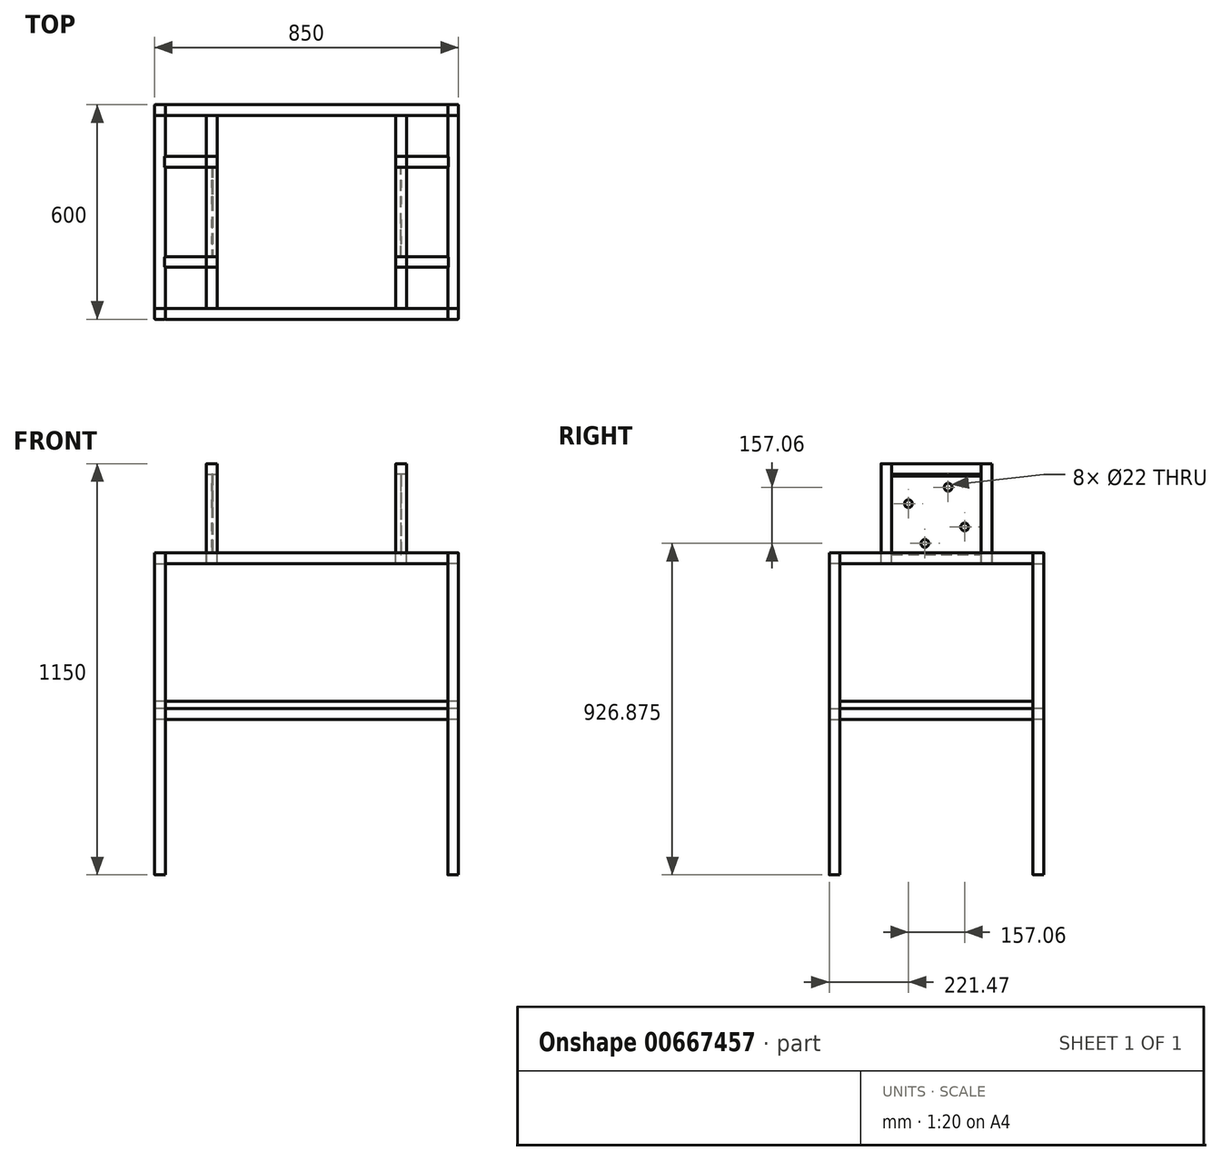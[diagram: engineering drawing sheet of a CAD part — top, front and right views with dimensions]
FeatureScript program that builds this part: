
annotation { "Feature Type Name" : "Feature", "Feature Type Description" : "" }
export const myFeature = defineFeature(function(context is Context, id is Id, definition is map)
    precondition{}
    {
        {
            var Q0;
            Q0=qCreatedBy(makeId("Top.planeOp"),FACE);
            var sketch = newSketch(context, id + "F0", { "sketchPlane" : qUnion([Q0])});
            skLineSegment(sketch, "E0.bottom", {"start": v(410, 285) * mm, "end": v(-410, 285) * mm, "construction": true});
            skLineSegment(sketch, "E0.left", {"start": v(410, 285) * mm, "end": v(410, -285) * mm, "construction": true});
            skLineSegment(sketch, "E0.right", {"start": v(-410, 285) * mm, "end": v(-410, -285) * mm, "construction": true});
            skPoint(sketch, "E0.middle", {"position": v(0, 0) * mm});
            skLineSegment(sketch, "E1.bottom", {"start": v(-395, 300) * mm, "end": v(-425, 300) * mm});
            skLineSegment(sketch, "E1.top", {"start": v(-395, 270) * mm, "end": v(-425, 270) * mm});
            skLineSegment(sketch, "E1.left", {"start": v(-395, 300) * mm, "end": v(-395, 270) * mm});
            skLineSegment(sketch, "E1.right", {"start": v(-425, 300) * mm, "end": v(-425, 270) * mm});
            skPoint(sketch, "E1.middle", {"position": v(-410, 285) * mm});
            skLineSegment(sketch, "E2", {"start": v(0, 0) * mm, "end": v(0, 285) * mm, "construction": true});
            skLineSegment(sketch, "E3", {"start": v(-410, 0) * mm, "end": v(410, 0) * mm, "construction": true});
            skLineSegment(sketch, "E4.MirrorCS", {"start": v(395, 270) * mm, "end": v(425, 270) * mm});
            skLineSegment(sketch, "E5.MirrorCS", {"start": v(395, 300) * mm, "end": v(395, 270) * mm});
            skLineSegment(sketch, "E6.MirrorCS", {"start": v(425, 300) * mm, "end": v(425, 270) * mm});
            skLineSegment(sketch, "E7.MirrorCS", {"start": v(395, 300) * mm, "end": v(425, 300) * mm});
            skLineSegment(sketch, "E8.MirrorCS", {"start": v(-395, -300) * mm, "end": v(-425, -300) * mm});
            skLineSegment(sketch, "E9.MirrorCS", {"start": v(-425, -300) * mm, "end": v(-425, -270) * mm});
            skLineSegment(sketch, "E10.MirrorCS", {"start": v(-395, -270) * mm, "end": v(-425, -270) * mm});
            skLineSegment(sketch, "E11.MirrorCS", {"start": v(-395, -300) * mm, "end": v(-395, -270) * mm});
            skLineSegment(sketch, "E12.MirrorCS", {"start": v(395, -270) * mm, "end": v(425, -270) * mm});
            skLineSegment(sketch, "E13.MirrorCS", {"start": v(395, -300) * mm, "end": v(395, -270) * mm});
            skLineSegment(sketch, "E14.MirrorCS", {"start": v(395, -300) * mm, "end": v(425, -300) * mm});
            skLineSegment(sketch, "E15.MirrorCS", {"start": v(425, -300) * mm, "end": v(425, -270) * mm});
            skSolve(sketch);
        }
        {
            var Q0;
            Q0 = qSketchRegion(id + "F0", true);
            extrude(context, id + "F1", {"entities" : qUnion([Q0]), "oppositeDirection" : true, "depth" : 900 * mm, "offsetDistance" : 25 * mm});
        }
        {
            var Q0;
            Q0=makeQuery(id+"F1.opExtrude","SWEPT_FACE",FACE,{"disambiguationData":[OSD([sQuery(id+"F0.wireOp",EDGE,"E13.MirrorCS")])]});
            var sketch = newSketch(context, id + "F2", { "sketchPlane" : qUnion([Q0])});
            skLineSegment(sketch, "E16.bottom", {"start": v(270, -465) * mm, "end": v(300, -465) * mm});
            skLineSegment(sketch, "E16.top", {"start": v(270, -435) * mm, "end": v(300, -435) * mm});
            skLineSegment(sketch, "E16.left", {"start": v(270, -465) * mm, "end": v(270, -435) * mm});
            skLineSegment(sketch, "E16.right", {"start": v(300, -465) * mm, "end": v(300, -435) * mm});
            skPoint(sketch, "E16.middle", {"position": v(285, -450) * mm});
            skSolve(sketch);
        }
        {
            var Q0;
            Q0 = qSketchRegion(id + "F2", true);
            extrude(context, id + "F3", {"entities" : qUnion([Q0]), "endBound" : BoundingType.UP_TO_NEXT, "depth" : 782 * mm, "offsetDistance" : 25 * mm});
        }
        {
            var Q0;
            Q0=makeQuery(id+"F1.opExtrude","SWEPT_FACE",FACE,{"disambiguationData":[OSD([sQuery(id+"F0.wireOp",EDGE,"E12.MirrorCS")])]});
            var sketch = newSketch(context, id + "F4", { "sketchPlane" : qUnion([Q0])});
            skLineSegment(sketch, "E17.bottom", {"start": v(-395, -465) * mm, "end": v(-425, -465) * mm});
            skLineSegment(sketch, "E17.top", {"start": v(-395, -435) * mm, "end": v(-425, -435) * mm});
            skLineSegment(sketch, "E17.left", {"start": v(-395, -465) * mm, "end": v(-395, -435) * mm});
            skLineSegment(sketch, "E17.right", {"start": v(-425, -465) * mm, "end": v(-425, -435) * mm});
            skSolve(sketch);
        }
        {
            var Q0;
            Q0=makeQuery(id+"F4.imprint","IMPRINT",FACE,{"disambiguationData":[TD([[makeQuery(id+"F4.imprint","IMPRINT",EDGE,{"derivedFrom":sQuery(id+"F4.wireOp",EDGE,"E17.bottom")}),-1.0]])]});
            extrude(context, id + "F5", {"entities" : qUnion([Q0]), "endBound" : BoundingType.UP_TO_NEXT, "depth" : 25 * mm, "offsetDistance" : 25 * mm});
        }
        {
            var Q0;
            Q0=makeQuery(id+"F1.opExtrude","SWEPT_FACE",FACE,{"disambiguationData":[OSD([sQuery(id+"F0.wireOp",EDGE,"E5.MirrorCS")])]});
            var sketch = newSketch(context, id + "F6", { "sketchPlane" : qUnion([Q0])});
            skLineSegment(sketch, "E18.bottom", {"start": v(-300, -435) * mm, "end": v(-270, -435) * mm});
            skLineSegment(sketch, "E18.top", {"start": v(-300, -465) * mm, "end": v(-270, -465) * mm});
            skLineSegment(sketch, "E18.left", {"start": v(-300, -435) * mm, "end": v(-300, -465) * mm});
            skLineSegment(sketch, "E18.right", {"start": v(-270, -435) * mm, "end": v(-270, -465) * mm});
            skSolve(sketch);
        }
        {
            var Q0;
            Q0=makeQuery(id+"F6.imprint","IMPRINT",FACE,{"disambiguationData":[TD([[makeQuery(id+"F6.imprint","IMPRINT",EDGE,{"derivedFrom":sQuery(id+"F6.wireOp",EDGE,"E18.bottom")}),-1.0]])]});
            extrude(context, id + "F7", {"entities" : qUnion([Q0]), "endBound" : BoundingType.UP_TO_NEXT, "depth" : 25 * mm, "offsetDistance" : 25 * mm});
        }
        {
            var Q0;
            Q0=makeQuery(id+"F1.opExtrude","SWEPT_FACE",FACE,{"disambiguationData":[OSD([sQuery(id+"F0.wireOp",EDGE,"E10.MirrorCS")])]});
            var sketch = newSketch(context, id + "F8", { "sketchPlane" : qUnion([Q0])});
            skLineSegment(sketch, "E19.bottom", {"start": v(395, -435) * mm, "end": v(425, -435) * mm});
            skLineSegment(sketch, "E19.top", {"start": v(395, -465) * mm, "end": v(425, -465) * mm});
            skLineSegment(sketch, "E19.left", {"start": v(395, -435) * mm, "end": v(395, -465) * mm});
            skLineSegment(sketch, "E19.right", {"start": v(425, -435) * mm, "end": v(425, -465) * mm});
            skSolve(sketch);
        }
        {
            var Q0;
            Q0=makeQuery(id+"F8.imprint","IMPRINT",FACE,{"disambiguationData":[TD([[makeQuery(id+"F8.imprint","IMPRINT",EDGE,{"derivedFrom":sQuery(id+"F8.wireOp",EDGE,"E19.bottom")}),-1.0]])]});
            extrude(context, id + "F9", {"entities" : qUnion([Q0]), "endBound" : BoundingType.UP_TO_NEXT, "depth" : 25 * mm, "offsetDistance" : 25 * mm});
        }
        {
            var Q0;
            Q0=makeQuery(id+"F1.opExtrude","SWEPT_FACE",FACE,{"disambiguationData":[OSD([sQuery(id+"F0.wireOp",EDGE,"E4.MirrorCS")])]});
            var sketch = newSketch(context, id + "F10", { "sketchPlane" : qUnion([Q0])});
            skLineSegment(sketch, "E20.bottom", {"start": v(425, -900) * mm, "end": v(395, -900) * mm});
            skLineSegment(sketch, "E20.top", {"start": v(425, -870) * mm, "end": v(395, -870) * mm});
            skLineSegment(sketch, "E20.left", {"start": v(425, -900) * mm, "end": v(425, -870) * mm});
            skLineSegment(sketch, "E20.right", {"start": v(395, -900) * mm, "end": v(395, -870) * mm});
            skSolve(sketch);
        }
        {
            var Q0;
            Q0 = qSketchRegion(id + "F10", true);
            extrude(context, id + "F11", {"entities" : qUnion([Q0]), "endBound" : BoundingType.UP_TO_NEXT, "depth" : 25 * mm, "offsetDistance" : 25 * mm});
        }
        {
            var Q0;
            Q0=makeQuery(id+"F1.opExtrude","SWEPT_FACE",FACE,{"disambiguationData":[OSD([sQuery(id+"F0.wireOp",EDGE,"E13.MirrorCS")])]});
            var sketch = newSketch(context, id + "F12", { "sketchPlane" : qUnion([Q0])});
            skLineSegment(sketch, "E21.bottom", {"start": v(300, -900) * mm, "end": v(270, -900) * mm});
            skLineSegment(sketch, "E21.top", {"start": v(300, -870) * mm, "end": v(270, -870) * mm});
            skLineSegment(sketch, "E21.left", {"start": v(300, -900) * mm, "end": v(300, -870) * mm});
            skLineSegment(sketch, "E21.right", {"start": v(270, -900) * mm, "end": v(270, -870) * mm});
            skSolve(sketch);
        }
        {
            var Q0;
            Q0 = qSketchRegion(id + "F12", true);
            extrude(context, id + "F13", {"entities" : qUnion([Q0]), "endBound" : BoundingType.UP_TO_NEXT, "depth" : 25 * mm, "offsetDistance" : 25 * mm});
        }
        {
            var Q0;
            Q0=makeQuery(id+"F1.opExtrude","SWEPT_FACE",FACE,{"disambiguationData":[OSD([sQuery(id+"F0.wireOp",EDGE,"E10.MirrorCS")])]});
            var sketch = newSketch(context, id + "F14", { "sketchPlane" : qUnion([Q0])});
            skLineSegment(sketch, "E22.bottom", {"start": v(425, -900) * mm, "end": v(395, -900) * mm});
            skLineSegment(sketch, "E22.top", {"start": v(425, -870) * mm, "end": v(395, -870) * mm});
            skLineSegment(sketch, "E22.left", {"start": v(425, -900) * mm, "end": v(425, -870) * mm});
            skLineSegment(sketch, "E22.right", {"start": v(395, -900) * mm, "end": v(395, -870) * mm});
            skSolve(sketch);
        }
        {
            var Q0;
            Q0 = qSketchRegion(id + "F14", true);
            var Q1;
            Q1=makeQuery(id+"F14.imprint","IMPRINT",FACE,{"disambiguationData":[TD([[makeQuery(id+"F14.imprint","IMPRINT",EDGE,{"derivedFrom":sQuery(id+"F14.wireOp",EDGE,"E22.bottom")}),1.0]])]});
            extrude(context, id + "F15", {"entities" : qUnion([Q0, Q1]), "endBound" : BoundingType.UP_TO_NEXT, "depth" : 25 * mm, "offsetDistance" : 25 * mm});
        }
        {
            var Q0;
            Q0=makeQuery(id+"F1.opExtrude","SWEPT_FACE",FACE,{"disambiguationData":[OSD([sQuery(id+"F0.wireOp",EDGE,"E1.left")])]});
            var sketch = newSketch(context, id + "F16", { "sketchPlane" : qUnion([Q0])});
            skLineSegment(sketch, "E23.bottom", {"start": v(300, -900) * mm, "end": v(270, -900) * mm});
            skLineSegment(sketch, "E23.top", {"start": v(300, -870) * mm, "end": v(270, -870) * mm});
            skLineSegment(sketch, "E23.left", {"start": v(300, -900) * mm, "end": v(300, -870) * mm});
            skLineSegment(sketch, "E23.right", {"start": v(270, -900) * mm, "end": v(270, -870) * mm});
            skSolve(sketch);
        }
        {
            var Q0;
            Q0 = qSketchRegion(id + "F16", true);
            var Q1;
            Q1=makeQuery(id+"F16.imprint","IMPRINT",FACE,{"disambiguationData":[TD([[makeQuery(id+"F16.imprint","IMPRINT",EDGE,{"derivedFrom":sQuery(id+"F16.wireOp",EDGE,"E23.bottom")}),-1.0]])]});
            extrude(context, id + "F17", {"entities" : qUnion([Q0, Q1]), "endBound" : BoundingType.UP_TO_NEXT, "depth" : 25 * mm, "offsetDistance" : 25 * mm});
        }
        {
            var Q0;
            Q0=makeQuery(id+"F13.opExtrude","SWEPT_FACE",FACE,{"disambiguationData":[OSD([sQuery(id+"F12.wireOp",EDGE,"E21.right")])]});
            var sketch = newSketch(context, id + "F18", { "sketchPlane" : qUnion([Q0])});
            skLineSegment(sketch, "E24.bottom", {"start": v(280, -900) * mm, "end": v(250, -900) * mm});
            skLineSegment(sketch, "E24.top", {"start": v(280, -870) * mm, "end": v(250, -870) * mm});
            skLineSegment(sketch, "E24.left", {"start": v(280, -900) * mm, "end": v(280, -870) * mm});
            skLineSegment(sketch, "E24.right", {"start": v(250, -900) * mm, "end": v(250, -870) * mm});
            skLineSegment(sketch, "E25.bottom", {"start": v(-250, -900) * mm, "end": v(-280, -900) * mm});
            skLineSegment(sketch, "E25.top", {"start": v(-250, -870) * mm, "end": v(-280, -870) * mm});
            skLineSegment(sketch, "E25.left", {"start": v(-250, -900) * mm, "end": v(-250, -870) * mm});
            skLineSegment(sketch, "E25.right", {"start": v(-280, -900) * mm, "end": v(-280, -870) * mm});
            skSolve(sketch);
        }
        {
            var Q0;
            Q0=makeQuery(id+"F18.imprint","IMPRINT",FACE,{"disambiguationData":[TD([[makeQuery(id+"F18.imprint","IMPRINT",EDGE,{"derivedFrom":sQuery(id+"F18.wireOp",EDGE,"E24.bottom")}),-1.0]])]});
            var Q1;
            Q1=makeQuery(id+"F18.imprint","IMPRINT",FACE,{"disambiguationData":[TD([[makeQuery(id+"F18.imprint","IMPRINT",EDGE,{"derivedFrom":sQuery(id+"F18.wireOp",EDGE,"E25.bottom")}),-1.0]])]});
            extrude(context, id + "F19", {"entities" : qUnion([Q0, Q1]), "endBound" : BoundingType.UP_TO_NEXT, "depth" : 25 * mm, "offsetDistance" : 25 * mm});
        }
        {
            var Q0;
            Q0=makeQuery(id+"F19.opExtrude","SWEPT_FACE",FACE,{"disambiguationData":[OSD([sQuery(id+"F18.wireOp",EDGE,"E24.right")])]});
            var sketch = newSketch(context, id + "F20", { "sketchPlane" : qUnion([Q0])});
            skLineSegment(sketch, "E26.bottom", {"start": v(155, -900) * mm, "end": v(125, -900) * mm});
            skLineSegment(sketch, "E26.top", {"start": v(155, -870) * mm, "end": v(125, -870) * mm});
            skLineSegment(sketch, "E26.left", {"start": v(155, -900) * mm, "end": v(155, -870) * mm});
            skLineSegment(sketch, "E26.right", {"start": v(125, -900) * mm, "end": v(125, -870) * mm});
            skLineSegment(sketch, "E27.bottom", {"start": v(-125, -900) * mm, "end": v(-155, -900) * mm});
            skLineSegment(sketch, "E27.top", {"start": v(-125, -870) * mm, "end": v(-155, -870) * mm});
            skLineSegment(sketch, "E27.left", {"start": v(-125, -900) * mm, "end": v(-125, -870) * mm});
            skLineSegment(sketch, "E27.right", {"start": v(-155, -900) * mm, "end": v(-155, -870) * mm});
            skSolve(sketch);
        }
        {
            var Q0;
            Q0=makeQuery(id+"F19.opExtrude","SWEPT_FACE",FACE,{"disambiguationData":[OSD([sQuery(id+"F18.wireOp",EDGE,"E24.bottom")])]});
            var sketch = newSketch(context, id + "F21", { "sketchPlane" : qUnion([Q0])});
            skLineSegment(sketch, "E28.bottom", {"start": v(-250, 155) * mm, "end": v(-280, 155) * mm});
            skLineSegment(sketch, "E28.top", {"start": v(-250, 125) * mm, "end": v(-280, 125) * mm});
            skLineSegment(sketch, "E28.left", {"start": v(-250, 155) * mm, "end": v(-250, 125) * mm});
            skLineSegment(sketch, "E28.right", {"start": v(-280, 155) * mm, "end": v(-280, 125) * mm});
            skLineSegment(sketch, "E29.bottom", {"start": v(-250, -125) * mm, "end": v(-280, -125) * mm});
            skLineSegment(sketch, "E29.top", {"start": v(-250, -155) * mm, "end": v(-280, -155) * mm});
            skLineSegment(sketch, "E29.left", {"start": v(-250, -125) * mm, "end": v(-250, -155) * mm});
            skLineSegment(sketch, "E29.right", {"start": v(-280, -125) * mm, "end": v(-280, -155) * mm});
            skSolve(sketch);
        }
        {
            var Q0;
            Q0=makeQuery(id+"F19.opExtrude","SWEPT_FACE",FACE,{"disambiguationData":[OSD([sQuery(id+"F18.wireOp",EDGE,"E25.bottom")])]});
            var sketch = newSketch(context, id + "F22", { "sketchPlane" : qUnion([Q0])});
            skLineSegment(sketch, "E30.bottom", {"start": v(250, -125) * mm, "end": v(280, -125) * mm});
            skLineSegment(sketch, "E30.top", {"start": v(250, -155) * mm, "end": v(280, -155) * mm});
            skLineSegment(sketch, "E30.left", {"start": v(250, -125) * mm, "end": v(250, -155) * mm});
            skLineSegment(sketch, "E30.right", {"start": v(280, -125) * mm, "end": v(280, -155) * mm});
            skLineSegment(sketch, "E31.bottom", {"start": v(250, 155) * mm, "end": v(280, 155) * mm});
            skLineSegment(sketch, "E31.top", {"start": v(250, 125) * mm, "end": v(280, 125) * mm});
            skLineSegment(sketch, "E31.left", {"start": v(250, 155) * mm, "end": v(250, 125) * mm});
            skLineSegment(sketch, "E31.right", {"start": v(280, 155) * mm, "end": v(280, 125) * mm});
            skSolve(sketch);
        }
        {
            var Q0;
            Q0=makeQuery(id+"F21.imprint","IMPRINT",FACE,{"disambiguationData":[TD([[makeQuery(id+"F21.imprint","IMPRINT",EDGE,{"derivedFrom":sQuery(id+"F21.wireOp",EDGE,"E28.bottom")}),1.0]])]});
            var Q1;
            Q1=makeQuery(id+"F22.imprint","IMPRINT",FACE,{"disambiguationData":[TD([[makeQuery(id+"F22.imprint","IMPRINT",EDGE,{"derivedFrom":sQuery(id+"F22.wireOp",EDGE,"E31.bottom")}),-1.0]])]});
            var Q2;
            Q2=makeQuery(id+"F21.imprint","IMPRINT",FACE,{"disambiguationData":[TD([[makeQuery(id+"F21.imprint","IMPRINT",EDGE,{"derivedFrom":sQuery(id+"F21.wireOp",EDGE,"E29.bottom")}),1.0]])]});
            var Q3;
            Q3=makeQuery(id+"F22.imprint","IMPRINT",FACE,{"disambiguationData":[TD([[makeQuery(id+"F22.imprint","IMPRINT",EDGE,{"derivedFrom":sQuery(id+"F22.wireOp",EDGE,"E30.bottom")}),-1.0]])]});
            extrude(context, id + "F23", {"entities" : qUnion([Q0, Q1, Q2, Q3]), "depth" : 250 * mm, "offsetDistance" : 25 * mm});
        }
        {
            var Q0;
            Q0=makeQuery(id+"F23.opExtrude","SWEPT_FACE",FACE,{"disambiguationData":[OSD([sQuery(id+"F21.wireOp",EDGE,"E29.bottom")])]});
            var sketch = newSketch(context, id + "F24", { "sketchPlane" : qUnion([Q0])});
            skLineSegment(sketch, "E32.bottom", {"start": v(-250, -1150) * mm, "end": v(-280, -1150) * mm});
            skLineSegment(sketch, "E32.top", {"start": v(-250, -1120) * mm, "end": v(-280, -1120) * mm});
            skLineSegment(sketch, "E32.left", {"start": v(-250, -1150) * mm, "end": v(-250, -1120) * mm});
            skLineSegment(sketch, "E32.right", {"start": v(-280, -1150) * mm, "end": v(-280, -1120) * mm});
            skSolve(sketch);
        }
        {
            var Q0;
            Q0=makeQuery(id+"F24.imprint","IMPRINT",FACE,{"disambiguationData":[TD([[makeQuery(id+"F24.imprint","IMPRINT",EDGE,{"derivedFrom":sQuery(id+"F24.wireOp",EDGE,"E32.bottom")}),-1.0]])]});
            extrude(context, id + "F25", {"entities" : qUnion([Q0]), "endBound" : BoundingType.UP_TO_NEXT, "depth" : 25 * mm, "offsetDistance" : 25 * mm});
        }
        {
            var Q0;
            Q0=makeQuery(id+"F23.opExtrude","SWEPT_FACE",FACE,{"disambiguationData":[OSD([sQuery(id+"F22.wireOp",EDGE,"E30.bottom")])]});
            var sketch = newSketch(context, id + "F26", { "sketchPlane" : qUnion([Q0])});
            skLineSegment(sketch, "E33.bottom", {"start": v(280, -1150) * mm, "end": v(250, -1150) * mm});
            skLineSegment(sketch, "E33.top", {"start": v(280, -1120) * mm, "end": v(250, -1120) * mm});
            skLineSegment(sketch, "E33.left", {"start": v(280, -1150) * mm, "end": v(280, -1120) * mm});
            skLineSegment(sketch, "E33.right", {"start": v(250, -1150) * mm, "end": v(250, -1120) * mm});
            skSolve(sketch);
        }
        {
            var Q0;
            Q0=makeQuery(id+"F26.imprint","IMPRINT",FACE,{"disambiguationData":[TD([[makeQuery(id+"F26.imprint","IMPRINT",EDGE,{"derivedFrom":sQuery(id+"F26.wireOp",EDGE,"E33.bottom")}),1.0]])]});
            extrude(context, id + "F27", {"entities" : qUnion([Q0]), "endBound" : BoundingType.UP_TO_NEXT, "depth" : 25 * mm, "offsetDistance" : 25 * mm});
        }
        {
            var Q0;
            Q0=makeQuery(id+"F23.opExtrude","CAP_EDGE",EDGE,{"disambiguationData":[OSD([sQuery(id+"F22.wireOp",EDGE,"E30.bottom")])],"isStart":true});
            cPoint(context, id + "F28", {"entities" : qUnion([Q0]), "parameter" : 0.5});
        }
        {
            var Q0;
            Q0=makeQuery(id+"F27.opExtrude","CAP_EDGE",EDGE,{"disambiguationData":[OSD([sQuery(id+"F26.wireOp",EDGE,"E33.top")])],"isStart":false});
            cPoint(context, id + "F29", {"entities" : qUnion([Q0]), "parameter" : 0.5});
        }
        {
            var Q0;
            Q0=makeQuery(id+"F27.opExtrude","CAP_EDGE",EDGE,{"disambiguationData":[OSD([sQuery(id+"F26.wireOp",EDGE,"E33.top")])],"isStart":true});
            cPoint(context, id + "F30", {"entities" : qUnion([Q0]), "parameter" : 0.5});
        }
        {
            var Q0;
            Q0 = qCreatedBy(id + "F28" ,VERTEX);
            var Q1;
            Q1 = qCreatedBy(id + "F29" ,VERTEX);
            var Q2;
            Q2 = qCreatedBy(id + "F30" ,VERTEX);
            cPlane(context, id + "F31", {"entities" : qUnion([Q0, Q1, Q2]), "cplaneType" : CPlaneType.THREE_POINT, "offset" : 25 * mm, "width" : 150 * mm, "height" : 150 * mm});
        }
        {
            var Q0;
            Q0=qCreatedBy(id+"F31.planeOp",FACE);
            var sketch = newSketch(context, id + "F32", { "sketchPlane" : qUnion([Q0])});
            skLineSegment(sketch, "E34.bottom", {"start": v(-125, -1115.4) * mm, "end": v(125, -1115.4) * mm});
            skLineSegment(sketch, "E34.top", {"start": v(-125, -895.4) * mm, "end": v(125, -895.4) * mm});
            skLineSegment(sketch, "E34.left", {"start": v(-125, -1115.4) * mm, "end": v(-125, -895.4) * mm});
            skLineSegment(sketch, "E34.right", {"start": v(125, -1115.4) * mm, "end": v(125, -895.4) * mm});
            skSolve(sketch);
        }
        {
            var Q0;
            Q0=makeQuery(id+"F32.imprint","IMPRINT",FACE,{"disambiguationData":[TD([[makeQuery(id+"F32.imprint","IMPRINT",EDGE,{"derivedFrom":sQuery(id+"F32.wireOp",EDGE,"E34.bottom")}),1.0]])]});
            extrude(context, id + "F33", {"entities" : qUnion([Q0]), "depth" : 2 * mm, "offsetDistance" : 25 * mm});
        }
        {
            var Q0;
            Q0=makeQuery(id+"F33.opExtrude","SWEPT_FACE",FACE,{"disambiguationData":[OSD([sQuery(id+"F32.wireOp",EDGE,"E34.bottom")])]});
            extrude(context, id + "F34", {"entities" : qUnion([Q0]), "endBound" : BoundingType.UP_TO_NEXT, "depth" : 25 * mm, "offsetDistance" : 25 * mm});
        }
        {
            var Q0;
            Q0=makeQuery(id+"F25.opExtrude","CAP_EDGE",EDGE,{"disambiguationData":[OSD([sQuery(id+"F24.wireOp",EDGE,"E32.top")])],"isStart":true});
            cPoint(context, id + "F35", {"entities" : qUnion([Q0]), "parameter" : 0.5});
        }
        {
            var Q0;
            Q0=makeQuery(id+"F25.opExtrude","CAP_EDGE",EDGE,{"disambiguationData":[OSD([sQuery(id+"F24.wireOp",EDGE,"E32.top")])],"isStart":false});
            cPoint(context, id + "F36", {"entities" : qUnion([Q0]), "parameter" : 0.5});
        }
        {
            var Q0;
            Q0=makeQuery(id+"F23.opExtrude","CAP_EDGE",EDGE,{"disambiguationData":[OSD([sQuery(id+"F21.wireOp",EDGE,"E28.top")])],"isStart":true});
            cPoint(context, id + "F37", {"entities" : qUnion([Q0]), "parameter" : 0.5});
        }
        {
            var Q0;
            Q0 = qCreatedBy(id + "F35" ,VERTEX);
            var Q1;
            Q1 = qCreatedBy(id + "F36" ,VERTEX);
            var Q2;
            Q2 = qCreatedBy(id + "F37" ,VERTEX);
            cPlane(context, id + "F38", {"entities" : qUnion([Q0, Q1, Q2]), "cplaneType" : CPlaneType.THREE_POINT, "offset" : 25 * mm, "width" : 150 * mm, "height" : 150 * mm});
        }
        {
            var Q0;
            Q0=qCreatedBy(id+"F38.planeOp",FACE);
            var sketch = newSketch(context, id + "F39", { "sketchPlane" : qUnion([Q0])});
            skLineSegment(sketch, "E35.bottom", {"start": v(-125, -1120) * mm, "end": v(125, -1120) * mm});
            skLineSegment(sketch, "E35.top", {"start": v(-125, -900) * mm, "end": v(125, -900) * mm});
            skLineSegment(sketch, "E35.left", {"start": v(-125, -1120) * mm, "end": v(-125, -900) * mm});
            skLineSegment(sketch, "E35.right", {"start": v(125, -1120) * mm, "end": v(125, -900) * mm});
            skSolve(sketch);
        }
        {
            var Q0;
            Q0 = qSketchRegion(id + "F39", true);
            var Q1;
            Q1=makeQuery(id+"F39.imprint","IMPRINT",FACE,{"disambiguationData":[TD([[makeQuery(id+"F39.imprint","IMPRINT",EDGE,{"derivedFrom":sQuery(id+"F39.wireOp",EDGE,"E35.bottom")}),1.0]])]});
            extrude(context, id + "F40", {"entities" : qUnion([Q0, Q1]), "depth" : 2 * mm, "offsetDistance" : 25 * mm});
        }
        {
            var Q0;
            Q0=makeQuery(id+"F9.opExtrude","SWEPT_FACE",FACE,{"disambiguationData":[OSD([sQuery(id+"F8.wireOp",EDGE,"E19.right")])]});
            var sketch = newSketch(context, id + "F41", { "sketchPlane" : qUnion([Q0])});
            skLineSegment(sketch, "E36.bottom", {"start": v(270, -465) * mm, "end": v(-270, -465) * mm});
            skLineSegment(sketch, "E36.top", {"start": v(270, -485) * mm, "end": v(-270, -485) * mm});
            skLineSegment(sketch, "E36.left", {"start": v(270, -465) * mm, "end": v(270, -485) * mm});
            skLineSegment(sketch, "E36.right", {"start": v(-270, -465) * mm, "end": v(-270, -485) * mm});
            skSolve(sketch);
        }
        {
            var Q0;
            Q0=makeQuery(id+"F41.imprint","IMPRINT",FACE,{"disambiguationData":[TD([[makeQuery(id+"F41.imprint","IMPRINT",EDGE,{"derivedFrom":sQuery(id+"F41.wireOp",EDGE,"E36.bottom")}),-1.0]])]});
            extrude(context, id + "F42", {"entities" : qUnion([Q0]), "oppositeDirection" : true, "depth" : 850 * mm, "offsetDistance" : 25 * mm});
        }
        {
            var Q0;
            Q0=makeQuery(id+"FFzUMfXQeQxxDpQ_17.opExtrude","SWEPT_BODY",BODY,{"disambiguationData":[OSD([sQuery(id+"F20.wireOp",EDGE,"E26.bottom"),sQuery(id+"F20.wireOp",EDGE,"E26.top"),sQuery(id+"F20.wireOp",EDGE,"E26.left"),sQuery(id+"F20.wireOp",EDGE,"E26.right")])]});
            var Q1;
            Q1=makeQuery(id+"F1.opExtrude","SWEPT_BODY",BODY,{"disambiguationData":[OSD([sQuery(id+"F0.wireOp",EDGE,"E1.bottom"),sQuery(id+"F0.wireOp",EDGE,"E1.top"),sQuery(id+"F0.wireOp",EDGE,"E1.left"),sQuery(id+"F0.wireOp",EDGE,"E1.right")])]});
            var Q2;
            Q2=makeQuery(id+"FFzUMfXQeQxxDpQ_17.opExtrude","SWEPT_BODY",BODY,{"disambiguationData":[OSD([sQuery(id+"F20.wireOp",EDGE,"E27.bottom"),sQuery(id+"F20.wireOp",EDGE,"E27.top"),sQuery(id+"F20.wireOp",EDGE,"E27.left"),sQuery(id+"F20.wireOp",EDGE,"E27.right")])]});
            var Q3;
            Q3=makeQuery(id+"F1.opExtrude","SWEPT_BODY",BODY,{"disambiguationData":[OSD([sQuery(id+"F0.wireOp",EDGE,"E4.MirrorCS"),sQuery(id+"F0.wireOp",EDGE,"E5.MirrorCS"),sQuery(id+"F0.wireOp",EDGE,"E6.MirrorCS"),sQuery(id+"F0.wireOp",EDGE,"E7.MirrorCS")])]});
            var Q4;
            Q4=makeQuery(id+"F5.opExtrude","SWEPT_BODY",BODY,{"disambiguationData":[OSD([sQuery(id+"F4.wireOp",EDGE,"E17.bottom"),sQuery(id+"F4.wireOp",EDGE,"E17.top"),sQuery(id+"F4.wireOp",EDGE,"E17.left"),sQuery(id+"F4.wireOp",EDGE,"E17.right")])]});
            var Q5;
            Q5=makeQuery(id+"F1.opExtrude","SWEPT_BODY",BODY,{"disambiguationData":[OSD([sQuery(id+"F0.wireOp",EDGE,"E12.MirrorCS"),sQuery(id+"F0.wireOp",EDGE,"E13.MirrorCS"),sQuery(id+"F0.wireOp",EDGE,"E14.MirrorCS"),sQuery(id+"F0.wireOp",EDGE,"E15.MirrorCS")])]});
            var Q6;
            Q6=makeQuery(id+"F11.opExtrude","SWEPT_BODY",BODY,{"disambiguationData":[OSD([sQuery(id+"F10.wireOp",EDGE,"E20.bottom"),sQuery(id+"F10.wireOp",EDGE,"E20.top"),sQuery(id+"F10.wireOp",EDGE,"E20.left"),sQuery(id+"F10.wireOp",EDGE,"E20.right")])]});
            var Q7;
            Q7=makeQuery(id+"F7.opExtrude","SWEPT_BODY",BODY,{"disambiguationData":[OSD([sQuery(id+"F6.wireOp",EDGE,"E18.bottom"),sQuery(id+"F6.wireOp",EDGE,"E18.top"),sQuery(id+"F6.wireOp",EDGE,"E18.left"),sQuery(id+"F6.wireOp",EDGE,"E18.right")])]});
            var Q8;
            Q8=makeQuery(id+"F9.opExtrude","SWEPT_BODY",BODY,{"disambiguationData":[OSD([sQuery(id+"F8.wireOp",EDGE,"E19.bottom"),sQuery(id+"F8.wireOp",EDGE,"E19.top"),sQuery(id+"F8.wireOp",EDGE,"E19.left"),sQuery(id+"F8.wireOp",EDGE,"E19.right")])]});
            var Q9;
            Q9=makeQuery(id+"F17.opExtrude","SWEPT_BODY",BODY,{"disambiguationData":[OSD([sQuery(id+"F16.wireOp",EDGE,"E23.bottom"),sQuery(id+"F16.wireOp",EDGE,"E23.top"),sQuery(id+"F16.wireOp",EDGE,"E23.left"),sQuery(id+"F16.wireOp",EDGE,"E23.right")])]});
            var Q10;
            Q10=makeQuery(id+"F13.opExtrude","SWEPT_BODY",BODY,{"disambiguationData":[OSD([sQuery(id+"F12.wireOp",EDGE,"E21.bottom"),sQuery(id+"F12.wireOp",EDGE,"E21.top"),sQuery(id+"F12.wireOp",EDGE,"E21.left"),sQuery(id+"F12.wireOp",EDGE,"E21.right")])]});
            var Q11;
            Q11=makeQuery(id+"F23.opExtrude","SWEPT_BODY",BODY,{"disambiguationData":[OSD([sQuery(id+"F21.wireOp",EDGE,"E29.bottom"),sQuery(id+"F21.wireOp",EDGE,"E29.top"),sQuery(id+"F21.wireOp",EDGE,"E29.left"),sQuery(id+"F21.wireOp",EDGE,"E29.right")])]});
            var Q12;
            Q12=makeQuery(id+"F19.opExtrude","SWEPT_BODY",BODY,{"disambiguationData":[OSD([sQuery(id+"F18.wireOp",EDGE,"E24.bottom"),sQuery(id+"F18.wireOp",EDGE,"E24.top"),sQuery(id+"F18.wireOp",EDGE,"E24.left"),sQuery(id+"F18.wireOp",EDGE,"E24.right")])]});
            var Q13;
            Q13=makeQuery(id+"F23.opExtrude","SWEPT_BODY",BODY,{"disambiguationData":[OSD([sQuery(id+"F22.wireOp",EDGE,"E31.bottom"),sQuery(id+"F22.wireOp",EDGE,"E31.top"),sQuery(id+"F22.wireOp",EDGE,"E31.left"),sQuery(id+"F22.wireOp",EDGE,"E31.right")])]});
            var Q14;
            Q14=makeQuery(id+"F23.opExtrude","SWEPT_BODY",BODY,{"disambiguationData":[OSD([sQuery(id+"F21.wireOp",EDGE,"E28.bottom"),sQuery(id+"F21.wireOp",EDGE,"E28.top"),sQuery(id+"F21.wireOp",EDGE,"E28.left"),sQuery(id+"F21.wireOp",EDGE,"E28.right")])]});
            var Q15;
            Q15=makeQuery(id+"F19.opExtrude","SWEPT_BODY",BODY,{"disambiguationData":[OSD([sQuery(id+"F18.wireOp",EDGE,"E25.bottom"),sQuery(id+"F18.wireOp",EDGE,"E25.top"),sQuery(id+"F18.wireOp",EDGE,"E25.left"),sQuery(id+"F18.wireOp",EDGE,"E25.right")])]});
            var Q16;
            Q16=makeQuery(id+"F3.opExtrude","SWEPT_BODY",BODY,{"disambiguationData":[OSD([sQuery(id+"F2.wireOp",EDGE,"E16.bottom"),sQuery(id+"F2.wireOp",EDGE,"E16.top"),sQuery(id+"F2.wireOp",EDGE,"E16.left"),sQuery(id+"F2.wireOp",EDGE,"E16.right")])]});
            var Q17;
            Q17=makeQuery(id+"F25.opExtrude","SWEPT_BODY",BODY,{"disambiguationData":[OSD([sQuery(id+"F24.wireOp",EDGE,"E32.bottom"),sQuery(id+"F24.wireOp",EDGE,"E32.top"),sQuery(id+"F24.wireOp",EDGE,"E32.left"),sQuery(id+"F24.wireOp",EDGE,"E32.right")])]});
            var Q18;
            Q18=makeQuery(id+"F1.opExtrude","SWEPT_BODY",BODY,{"disambiguationData":[OSD([sQuery(id+"F0.wireOp",EDGE,"E8.MirrorCS"),sQuery(id+"F0.wireOp",EDGE,"E9.MirrorCS"),sQuery(id+"F0.wireOp",EDGE,"E10.MirrorCS"),sQuery(id+"F0.wireOp",EDGE,"E11.MirrorCS")])]});
            var Q19;
            Q19=makeQuery(id+"F23.opExtrude","SWEPT_BODY",BODY,{"disambiguationData":[OSD([sQuery(id+"F22.wireOp",EDGE,"E30.bottom"),sQuery(id+"F22.wireOp",EDGE,"E30.top"),sQuery(id+"F22.wireOp",EDGE,"E30.left"),sQuery(id+"F22.wireOp",EDGE,"E30.right")])]});
            var Q20;
            Q20=makeQuery(id+"F15.opExtrude","SWEPT_BODY",BODY,{"disambiguationData":[OSD([sQuery(id+"F14.wireOp",EDGE,"E22.bottom"),sQuery(id+"F14.wireOp",EDGE,"E22.top"),sQuery(id+"F14.wireOp",EDGE,"E22.left"),sQuery(id+"F14.wireOp",EDGE,"E22.right")])]});
            var Q21;
            Q21=makeQuery(id+"F27.opExtrude","SWEPT_BODY",BODY,{"disambiguationData":[OSD([sQuery(id+"F26.wireOp",EDGE,"E33.bottom"),sQuery(id+"F26.wireOp",EDGE,"E33.top"),sQuery(id+"F26.wireOp",EDGE,"E33.left"),sQuery(id+"F26.wireOp",EDGE,"E33.right")])]});
            var Q22;
            Q22=makeQuery(id+"F42.opExtrude","SWEPT_BODY",BODY,{"disambiguationData":[OSD([sQuery(id+"F41.wireOp",EDGE,"E36.bottom"),sQuery(id+"F41.wireOp",EDGE,"E36.top"),sQuery(id+"F41.wireOp",EDGE,"E36.left"),sQuery(id+"F41.wireOp",EDGE,"E36.right")])]});
            var Q23;
            Q23=makeQuery(id+"F40.opExtrude","SWEPT_BODY",BODY,{"disambiguationData":[OSD([sQuery(id+"F39.wireOp",EDGE,"E35.bottom"),sQuery(id+"F39.wireOp",EDGE,"E35.top"),sQuery(id+"F39.wireOp",EDGE,"E35.left"),sQuery(id+"F39.wireOp",EDGE,"E35.right")])]});
            var Q24;
            Q24=makeQuery(id+"F34.opExtrude","SWEPT_BODY",BODY,{"disambiguationData":[OSD([sQuery(id+"F32.wireOp",EDGE,"E34.bottom")])]});
            var Q25;
            Q25=makeQuery(id+"F33.opExtrude","SWEPT_BODY",BODY,{"disambiguationData":[OSD([sQuery(id+"F32.wireOp",EDGE,"E34.bottom"),sQuery(id+"F32.wireOp",EDGE,"E34.top"),sQuery(id+"F32.wireOp",EDGE,"E34.left"),sQuery(id+"F32.wireOp",EDGE,"E34.right")])]});
            var Q26;
            Q26=makeQuery(id+"F1.opExtrude","CAP_EDGE",EDGE,{"disambiguationData":[OSD([sQuery(id+"F0.wireOp",EDGE,"E8.MirrorCS")])],"isStart":true});
            transform(context, id + "F43", {"entities" : qUnion([Q0, Q1, Q2, Q3, Q4, Q5, Q6, Q7, Q8, Q9, Q10, Q11, Q12, Q13, Q14, Q15, Q16, Q17, Q18, Q19, Q20, Q21, Q22, Q23, Q24, Q25]), "transformType" : TransformType.ROTATION, "transformAxis" : qUnion([Q26]), "angle" : 180 * degree, "makeCopy" : false});
        }
        {
            var Q0;
            Q0=makeQuery(id+"FFzUMfXQeQxxDpQ_17.opExtrude","SWEPT_BODY",BODY,{"disambiguationData":[OSD([sQuery(id+"F20.wireOp",EDGE,"E26.bottom"),sQuery(id+"F20.wireOp",EDGE,"E26.top"),sQuery(id+"F20.wireOp",EDGE,"E26.left"),sQuery(id+"F20.wireOp",EDGE,"E26.right")])]});
            var Q1;
            Q1=makeQuery(id+"F1.opExtrude","SWEPT_BODY",BODY,{"disambiguationData":[OSD([sQuery(id+"F0.wireOp",EDGE,"E1.bottom"),sQuery(id+"F0.wireOp",EDGE,"E1.top"),sQuery(id+"F0.wireOp",EDGE,"E1.left"),sQuery(id+"F0.wireOp",EDGE,"E1.right")])]});
            var Q2;
            Q2=makeQuery(id+"F1.opExtrude","SWEPT_BODY",BODY,{"disambiguationData":[OSD([sQuery(id+"F0.wireOp",EDGE,"E4.MirrorCS"),sQuery(id+"F0.wireOp",EDGE,"E5.MirrorCS"),sQuery(id+"F0.wireOp",EDGE,"E6.MirrorCS"),sQuery(id+"F0.wireOp",EDGE,"E7.MirrorCS")])]});
            var Q3;
            Q3=makeQuery(id+"F5.opExtrude","SWEPT_BODY",BODY,{"disambiguationData":[OSD([sQuery(id+"F4.wireOp",EDGE,"E17.bottom"),sQuery(id+"F4.wireOp",EDGE,"E17.top"),sQuery(id+"F4.wireOp",EDGE,"E17.left"),sQuery(id+"F4.wireOp",EDGE,"E17.right")])]});
            var Q4;
            Q4=makeQuery(id+"F1.opExtrude","SWEPT_BODY",BODY,{"disambiguationData":[OSD([sQuery(id+"F0.wireOp",EDGE,"E12.MirrorCS"),sQuery(id+"F0.wireOp",EDGE,"E13.MirrorCS"),sQuery(id+"F0.wireOp",EDGE,"E14.MirrorCS"),sQuery(id+"F0.wireOp",EDGE,"E15.MirrorCS")])]});
            var Q5;
            Q5=makeQuery(id+"F11.opExtrude","SWEPT_BODY",BODY,{"disambiguationData":[OSD([sQuery(id+"F10.wireOp",EDGE,"E20.bottom"),sQuery(id+"F10.wireOp",EDGE,"E20.top"),sQuery(id+"F10.wireOp",EDGE,"E20.left"),sQuery(id+"F10.wireOp",EDGE,"E20.right")])]});
            var Q6;
            Q6=makeQuery(id+"F7.opExtrude","SWEPT_BODY",BODY,{"disambiguationData":[OSD([sQuery(id+"F6.wireOp",EDGE,"E18.bottom"),sQuery(id+"F6.wireOp",EDGE,"E18.top"),sQuery(id+"F6.wireOp",EDGE,"E18.left"),sQuery(id+"F6.wireOp",EDGE,"E18.right")])]});
            var Q7;
            Q7=makeQuery(id+"F9.opExtrude","SWEPT_BODY",BODY,{"disambiguationData":[OSD([sQuery(id+"F8.wireOp",EDGE,"E19.bottom"),sQuery(id+"F8.wireOp",EDGE,"E19.top"),sQuery(id+"F8.wireOp",EDGE,"E19.left"),sQuery(id+"F8.wireOp",EDGE,"E19.right")])]});
            var Q8;
            Q8=makeQuery(id+"F17.opExtrude","SWEPT_BODY",BODY,{"disambiguationData":[OSD([sQuery(id+"F16.wireOp",EDGE,"E23.bottom"),sQuery(id+"F16.wireOp",EDGE,"E23.top"),sQuery(id+"F16.wireOp",EDGE,"E23.left"),sQuery(id+"F16.wireOp",EDGE,"E23.right")])]});
            var Q9;
            Q9=makeQuery(id+"F13.opExtrude","SWEPT_BODY",BODY,{"disambiguationData":[OSD([sQuery(id+"F12.wireOp",EDGE,"E21.bottom"),sQuery(id+"F12.wireOp",EDGE,"E21.top"),sQuery(id+"F12.wireOp",EDGE,"E21.left"),sQuery(id+"F12.wireOp",EDGE,"E21.right")])]});
            var Q10;
            Q10=makeQuery(id+"F23.opExtrude","SWEPT_BODY",BODY,{"disambiguationData":[OSD([sQuery(id+"F21.wireOp",EDGE,"E29.bottom"),sQuery(id+"F21.wireOp",EDGE,"E29.top"),sQuery(id+"F21.wireOp",EDGE,"E29.left"),sQuery(id+"F21.wireOp",EDGE,"E29.right")])]});
            var Q11;
            Q11=makeQuery(id+"F19.opExtrude","SWEPT_BODY",BODY,{"disambiguationData":[OSD([sQuery(id+"F18.wireOp",EDGE,"E24.bottom"),sQuery(id+"F18.wireOp",EDGE,"E24.top"),sQuery(id+"F18.wireOp",EDGE,"E24.left"),sQuery(id+"F18.wireOp",EDGE,"E24.right")])]});
            var Q12;
            Q12=makeQuery(id+"F23.opExtrude","SWEPT_BODY",BODY,{"disambiguationData":[OSD([sQuery(id+"F22.wireOp",EDGE,"E31.bottom"),sQuery(id+"F22.wireOp",EDGE,"E31.top"),sQuery(id+"F22.wireOp",EDGE,"E31.left"),sQuery(id+"F22.wireOp",EDGE,"E31.right")])]});
            var Q13;
            Q13=makeQuery(id+"F23.opExtrude","SWEPT_BODY",BODY,{"disambiguationData":[OSD([sQuery(id+"F21.wireOp",EDGE,"E28.bottom"),sQuery(id+"F21.wireOp",EDGE,"E28.top"),sQuery(id+"F21.wireOp",EDGE,"E28.left"),sQuery(id+"F21.wireOp",EDGE,"E28.right")])]});
            var Q14;
            Q14=makeQuery(id+"F19.opExtrude","SWEPT_BODY",BODY,{"disambiguationData":[OSD([sQuery(id+"F18.wireOp",EDGE,"E25.bottom"),sQuery(id+"F18.wireOp",EDGE,"E25.top"),sQuery(id+"F18.wireOp",EDGE,"E25.left"),sQuery(id+"F18.wireOp",EDGE,"E25.right")])]});
            var Q15;
            Q15=makeQuery(id+"F3.opExtrude","SWEPT_BODY",BODY,{"disambiguationData":[OSD([sQuery(id+"F2.wireOp",EDGE,"E16.bottom"),sQuery(id+"F2.wireOp",EDGE,"E16.top"),sQuery(id+"F2.wireOp",EDGE,"E16.left"),sQuery(id+"F2.wireOp",EDGE,"E16.right")])]});
            var Q16;
            Q16=makeQuery(id+"F25.opExtrude","SWEPT_BODY",BODY,{"disambiguationData":[OSD([sQuery(id+"F24.wireOp",EDGE,"E32.bottom"),sQuery(id+"F24.wireOp",EDGE,"E32.top"),sQuery(id+"F24.wireOp",EDGE,"E32.left"),sQuery(id+"F24.wireOp",EDGE,"E32.right")])]});
            var Q17;
            Q17=makeQuery(id+"F1.opExtrude","SWEPT_BODY",BODY,{"disambiguationData":[OSD([sQuery(id+"F0.wireOp",EDGE,"E8.MirrorCS"),sQuery(id+"F0.wireOp",EDGE,"E9.MirrorCS"),sQuery(id+"F0.wireOp",EDGE,"E10.MirrorCS"),sQuery(id+"F0.wireOp",EDGE,"E11.MirrorCS")])]});
            var Q18;
            Q18=makeQuery(id+"F23.opExtrude","SWEPT_BODY",BODY,{"disambiguationData":[OSD([sQuery(id+"F22.wireOp",EDGE,"E30.bottom"),sQuery(id+"F22.wireOp",EDGE,"E30.top"),sQuery(id+"F22.wireOp",EDGE,"E30.left"),sQuery(id+"F22.wireOp",EDGE,"E30.right")])]});
            var Q19;
            Q19=makeQuery(id+"F15.opExtrude","SWEPT_BODY",BODY,{"disambiguationData":[OSD([sQuery(id+"F14.wireOp",EDGE,"E22.bottom"),sQuery(id+"F14.wireOp",EDGE,"E22.top"),sQuery(id+"F14.wireOp",EDGE,"E22.left"),sQuery(id+"F14.wireOp",EDGE,"E22.right")])]});
            var Q20;
            Q20=makeQuery(id+"F27.opExtrude","SWEPT_BODY",BODY,{"disambiguationData":[OSD([sQuery(id+"F26.wireOp",EDGE,"E33.bottom"),sQuery(id+"F26.wireOp",EDGE,"E33.top"),sQuery(id+"F26.wireOp",EDGE,"E33.left"),sQuery(id+"F26.wireOp",EDGE,"E33.right")])]});
            var Q21;
            Q21=makeQuery(id+"F42.opExtrude","SWEPT_BODY",BODY,{"disambiguationData":[OSD([sQuery(id+"F41.wireOp",EDGE,"E36.bottom"),sQuery(id+"F41.wireOp",EDGE,"E36.top"),sQuery(id+"F41.wireOp",EDGE,"E36.left"),sQuery(id+"F41.wireOp",EDGE,"E36.right")])]});
            var Q22;
            Q22=makeQuery(id+"F40.opExtrude","SWEPT_BODY",BODY,{"disambiguationData":[OSD([sQuery(id+"F39.wireOp",EDGE,"E35.bottom"),sQuery(id+"F39.wireOp",EDGE,"E35.top"),sQuery(id+"F39.wireOp",EDGE,"E35.left"),sQuery(id+"F39.wireOp",EDGE,"E35.right")])]});
            var Q23;
            Q23=makeQuery(id+"F33.opExtrude","SWEPT_BODY",BODY,{"disambiguationData":[OSD([sQuery(id+"F32.wireOp",EDGE,"E34.bottom"),sQuery(id+"F32.wireOp",EDGE,"E34.top"),sQuery(id+"F32.wireOp",EDGE,"E34.left"),sQuery(id+"F32.wireOp",EDGE,"E34.right")])]});
            var Q24;
            Q24=makeQuery(id+"FFzUMfXQeQxxDpQ_17.opExtrude","SWEPT_BODY",BODY,{"disambiguationData":[OSD([sQuery(id+"F20.wireOp",EDGE,"E27.bottom"),sQuery(id+"F20.wireOp",EDGE,"E27.top"),sQuery(id+"F20.wireOp",EDGE,"E27.left"),sQuery(id+"F20.wireOp",EDGE,"E27.right")])]});
            var Q25;
            Q25=makeQuery(id+"F34.opExtrude","SWEPT_BODY",BODY,{"disambiguationData":[OSD([sQuery(id+"F32.wireOp",EDGE,"E34.bottom")])]});
            transform(context, id + "F44", {"entities" : qUnion([Q0, Q1, Q2, Q3, Q4, Q5, Q6, Q7, Q8, Q9, Q10, Q11, Q12, Q13, Q14, Q15, Q16, Q17, Q18, Q19, Q20, Q21, Q22, Q23, Q24, Q25]), "transformType" : TransformType.TRANSLATION_3D, "dx" : 0 * mm, "dy" : 530 * mm, "dz" : 0 * mm, "makeCopy" : false});
        }
        {
            var Q0;
            Q0=makeQuery(id+"F17.opExtrude","SWEPT_EDGE",EDGE,{"disambiguationData":[OSD([sQuery(id+"F0.wireOp",EDGE,"E1.bottom"),sQuery(id+"F0.wireOp",EDGE,"E1.left"),sQuery(id+"F16.wireOp",EDGE,"E23.top"),sQuery(id+"F16.wireOp",EDGE,"E23.left")])]});
            var Q1;
            Q1=makeQuery(id+"F17.opExtrude","SWEPT_EDGE",EDGE,{"disambiguationData":[OSD([sQuery(id+"F16.wireOp",EDGE,"E23.bottom"),sQuery(id+"F16.wireOp",EDGE,"E23.left")])]});
            var Q2;
            Q2=makeQuery(id+"F1.opExtrude","SWEPT_EDGE",EDGE,{"disambiguationData":[OSD([sQuery(id+"F0.wireOp",EDGE,"E1.bottom"),sQuery(id+"F0.wireOp",EDGE,"E1.left")])]});
            var Q3;
            Q3=makeQuery(id+"F1.opExtrude","SWEPT_EDGE",EDGE,{"disambiguationData":[OSD([sQuery(id+"F0.wireOp",EDGE,"E1.bottom"),sQuery(id+"F0.wireOp",EDGE,"E1.right")])]});
            var Q4;
            Q4=makeQuery(id+"F1.opExtrude","SWEPT_EDGE",EDGE,{"disambiguationData":[OSD([sQuery(id+"F0.wireOp",EDGE,"E1.top"),sQuery(id+"F0.wireOp",EDGE,"E1.left")])]});
            var Q5;
            Q5=makeQuery(id+"F1.opExtrude","SWEPT_EDGE",EDGE,{"disambiguationData":[OSD([sQuery(id+"F0.wireOp",EDGE,"E5.MirrorCS"),sQuery(id+"F0.wireOp",EDGE,"E7.MirrorCS")])]});
            var Q6;
            Q6=makeQuery(id+"F1.opExtrude","SWEPT_EDGE",EDGE,{"disambiguationData":[OSD([sQuery(id+"F0.wireOp",EDGE,"E6.MirrorCS"),sQuery(id+"F0.wireOp",EDGE,"E7.MirrorCS")])]});
            var Q7;
            Q7=makeQuery(id+"F1.opExtrude","SWEPT_EDGE",EDGE,{"disambiguationData":[OSD([sQuery(id+"F0.wireOp",EDGE,"E4.MirrorCS"),sQuery(id+"F0.wireOp",EDGE,"E6.MirrorCS")])]});
            var Q8;
            Q8=makeQuery(id+"F7.opExtrude","SWEPT_EDGE",EDGE,{"disambiguationData":[OSD([sQuery(id+"F0.wireOp",EDGE,"E5.MirrorCS"),sQuery(id+"F0.wireOp",EDGE,"E7.MirrorCS"),sQuery(id+"F6.wireOp",EDGE,"E18.top"),sQuery(id+"F6.wireOp",EDGE,"E18.left")])]});
            var Q9;
            Q9=makeQuery(id+"F7.opExtrude","SWEPT_EDGE",EDGE,{"disambiguationData":[OSD([sQuery(id+"F0.wireOp",EDGE,"E5.MirrorCS"),sQuery(id+"F0.wireOp",EDGE,"E7.MirrorCS"),sQuery(id+"F6.wireOp",EDGE,"E18.bottom"),sQuery(id+"F6.wireOp",EDGE,"E18.left")])]});
            var Q10;
            Q10=makeQuery(id+"F17.opExtrude","SWEPT_EDGE",EDGE,{"disambiguationData":[OSD([sQuery(id+"F16.wireOp",EDGE,"E23.bottom"),sQuery(id+"F16.wireOp",EDGE,"E23.right")])]});
            var Q11;
            Q11=makeQuery(id+"F1.opExtrude","SWEPT_EDGE",EDGE,{"disambiguationData":[OSD([sQuery(id+"F0.wireOp",EDGE,"E1.top"),sQuery(id+"F0.wireOp",EDGE,"E1.right")])]});
            var Q12;
            Q12=makeQuery(id+"F1.opExtrude","SWEPT_EDGE",EDGE,{"disambiguationData":[OSD([sQuery(id+"F0.wireOp",EDGE,"E4.MirrorCS"),sQuery(id+"F0.wireOp",EDGE,"E5.MirrorCS")])]});
            var Q13;
            Q13=makeQuery(id+"F11.opExtrude","SWEPT_EDGE",EDGE,{"disambiguationData":[OSD([sQuery(id+"F0.wireOp",EDGE,"E4.MirrorCS"),sQuery(id+"F0.wireOp",EDGE,"E6.MirrorCS"),sQuery(id+"F10.wireOp",EDGE,"E20.top"),sQuery(id+"F10.wireOp",EDGE,"E20.left")])]});
            var Q14;
            Q14=makeQuery(id+"F11.opExtrude","SWEPT_EDGE",EDGE,{"disambiguationData":[OSD([sQuery(id+"F10.wireOp",EDGE,"E20.bottom"),sQuery(id+"F10.wireOp",EDGE,"E20.left")])]});
            var Q15;
            Q15=makeQuery(id+"F11.opExtrude","SWEPT_EDGE",EDGE,{"disambiguationData":[OSD([sQuery(id+"F10.wireOp",EDGE,"E20.bottom"),sQuery(id+"F10.wireOp",EDGE,"E20.right")])]});
            var Q16;
            Q16=makeQuery(id+"F1.opExtrude","SWEPT_EDGE",EDGE,{"disambiguationData":[OSD([sQuery(id+"F0.wireOp",EDGE,"E12.MirrorCS"),sQuery(id+"F0.wireOp",EDGE,"E13.MirrorCS")])]});
            var Q17;
            Q17=makeQuery(id+"F1.opExtrude","SWEPT_EDGE",EDGE,{"disambiguationData":[OSD([sQuery(id+"F0.wireOp",EDGE,"E12.MirrorCS"),sQuery(id+"F0.wireOp",EDGE,"E15.MirrorCS")])]});
            var Q18;
            Q18=makeQuery(id+"F1.opExtrude","SWEPT_EDGE",EDGE,{"disambiguationData":[OSD([sQuery(id+"F0.wireOp",EDGE,"E14.MirrorCS"),sQuery(id+"F0.wireOp",EDGE,"E15.MirrorCS")])]});
            var Q19;
            Q19=makeQuery(id+"F1.opExtrude","SWEPT_EDGE",EDGE,{"disambiguationData":[OSD([sQuery(id+"F0.wireOp",EDGE,"E13.MirrorCS"),sQuery(id+"F0.wireOp",EDGE,"E14.MirrorCS")])]});
            var Q20;
            Q20=makeQuery(id+"F13.opExtrude","SWEPT_EDGE",EDGE,{"disambiguationData":[OSD([sQuery(id+"F0.wireOp",EDGE,"E13.MirrorCS"),sQuery(id+"F0.wireOp",EDGE,"E14.MirrorCS"),sQuery(id+"F12.wireOp",EDGE,"E21.top"),sQuery(id+"F12.wireOp",EDGE,"E21.left")])]});
            var Q21;
            Q21=makeQuery(id+"F13.opExtrude","SWEPT_EDGE",EDGE,{"disambiguationData":[OSD([sQuery(id+"F12.wireOp",EDGE,"E21.bottom"),sQuery(id+"F12.wireOp",EDGE,"E21.left")])]});
            var Q22;
            Q22=makeQuery(id+"F13.opExtrude","SWEPT_EDGE",EDGE,{"disambiguationData":[OSD([sQuery(id+"F0.wireOp",EDGE,"E12.MirrorCS"),sQuery(id+"F0.wireOp",EDGE,"E13.MirrorCS"),sQuery(id+"F12.wireOp",EDGE,"E21.top"),sQuery(id+"F12.wireOp",EDGE,"E21.right")])]});
            var Q23;
            Q23=makeQuery(id+"F13.opExtrude","SWEPT_EDGE",EDGE,{"disambiguationData":[OSD([sQuery(id+"F12.wireOp",EDGE,"E21.bottom"),sQuery(id+"F12.wireOp",EDGE,"E21.right")])]});
            var Q24;
            Q24=makeQuery(id+"F19.opExtrude","SWEPT_EDGE",EDGE,{"disambiguationData":[OSD([sQuery(id+"F12.wireOp",EDGE,"E21.bottom"),sQuery(id+"F12.wireOp",EDGE,"E21.right"),sQuery(id+"F18.wireOp",EDGE,"E25.bottom"),sQuery(id+"F18.wireOp",EDGE,"E25.right")])]});
            var Q25;
            Q25=makeQuery(id+"F19.opExtrude","SWEPT_EDGE",EDGE,{"disambiguationData":[OSD([sQuery(id+"F12.wireOp",EDGE,"E21.bottom"),sQuery(id+"F12.wireOp",EDGE,"E21.right"),sQuery(id+"F18.wireOp",EDGE,"E25.bottom"),sQuery(id+"F18.wireOp",EDGE,"E25.left")])]});
            var Q26;
            Q26=makeQuery(id+"F19.opExtrude","SWEPT_EDGE",EDGE,{"disambiguationData":[OSD([sQuery(id+"F0.wireOp",EDGE,"E12.MirrorCS"),sQuery(id+"F0.wireOp",EDGE,"E13.MirrorCS"),sQuery(id+"F12.wireOp",EDGE,"E21.top"),sQuery(id+"F12.wireOp",EDGE,"E21.right"),sQuery(id+"F18.wireOp",EDGE,"E25.top"),sQuery(id+"F18.wireOp",EDGE,"E25.right")])]});
            var Q27;
            Q27=makeQuery(id+"F27.opExtrude","SWEPT_EDGE",EDGE,{"disambiguationData":[OSD([sQuery(id+"F26.wireOp",EDGE,"E33.bottom"),sQuery(id+"F26.wireOp",EDGE,"E33.left")])]});
            var Q28;
            Q28=makeQuery(id+"F27.opExtrude","SWEPT_EDGE",EDGE,{"disambiguationData":[OSD([sQuery(id+"F12.wireOp",EDGE,"E21.bottom"),sQuery(id+"F12.wireOp",EDGE,"E21.right"),sQuery(id+"F18.wireOp",EDGE,"E25.bottom"),sQuery(id+"F18.wireOp",EDGE,"E25.right"),sQuery(id+"F22.wireOp",EDGE,"E30.bottom"),sQuery(id+"F22.wireOp",EDGE,"E30.right"),sQuery(id+"F26.wireOp",EDGE,"E33.top"),sQuery(id+"F26.wireOp",EDGE,"E33.left")])]});
            var Q29;
            Q29=makeQuery(id+"F23.opExtrude","SWEPT_EDGE",EDGE,{"disambiguationData":[OSD([sQuery(id+"F12.wireOp",EDGE,"E21.bottom"),sQuery(id+"F12.wireOp",EDGE,"E21.right"),sQuery(id+"F18.wireOp",EDGE,"E25.bottom"),sQuery(id+"F18.wireOp",EDGE,"E25.right"),sQuery(id+"F22.wireOp",EDGE,"E30.bottom"),sQuery(id+"F22.wireOp",EDGE,"E30.right")])]});
            var Q30;
            Q30=makeQuery(id+"F23.opExtrude","SWEPT_EDGE",EDGE,{"disambiguationData":[OSD([sQuery(id+"F12.wireOp",EDGE,"E21.bottom"),sQuery(id+"F12.wireOp",EDGE,"E21.right"),sQuery(id+"F18.wireOp",EDGE,"E25.bottom"),sQuery(id+"F18.wireOp",EDGE,"E25.right"),sQuery(id+"F22.wireOp",EDGE,"E30.top"),sQuery(id+"F22.wireOp",EDGE,"E30.right")])]});
            var Q31;
            Q31=makeQuery(id+"F19.opExtrude","SWEPT_EDGE",EDGE,{"disambiguationData":[OSD([sQuery(id+"F12.wireOp",EDGE,"E21.bottom"),sQuery(id+"F12.wireOp",EDGE,"E21.right"),sQuery(id+"F18.wireOp",EDGE,"E24.bottom"),sQuery(id+"F18.wireOp",EDGE,"E24.right")])]});
            var Q32;
            Q32=makeQuery(id+"F19.opExtrude","SWEPT_EDGE",EDGE,{"disambiguationData":[OSD([sQuery(id+"F0.wireOp",EDGE,"E12.MirrorCS"),sQuery(id+"F0.wireOp",EDGE,"E13.MirrorCS"),sQuery(id+"F12.wireOp",EDGE,"E21.top"),sQuery(id+"F12.wireOp",EDGE,"E21.right"),sQuery(id+"F18.wireOp",EDGE,"E24.top"),sQuery(id+"F18.wireOp",EDGE,"E24.right")])]});
            var Q33;
            Q33=makeQuery(id+"FFzUMfXQeQxxDpQ_17.opExtrude","SWEPT_EDGE",EDGE,{"disambiguationData":[OSD([sQuery(id+"F12.wireOp",EDGE,"E21.bottom"),sQuery(id+"F12.wireOp",EDGE,"E21.right"),sQuery(id+"F18.wireOp",EDGE,"E24.bottom"),sQuery(id+"F18.wireOp",EDGE,"E24.right"),sQuery(id+"F20.wireOp",EDGE,"E26.bottom"),sQuery(id+"F20.wireOp",EDGE,"E26.left")])]});
            var Q34;
            Q34=makeQuery(id+"FFzUMfXQeQxxDpQ_17.opExtrude","SWEPT_EDGE",EDGE,{"disambiguationData":[OSD([sQuery(id+"F0.wireOp",EDGE,"E12.MirrorCS"),sQuery(id+"F0.wireOp",EDGE,"E13.MirrorCS"),sQuery(id+"F12.wireOp",EDGE,"E21.top"),sQuery(id+"F12.wireOp",EDGE,"E21.right"),sQuery(id+"F18.wireOp",EDGE,"E24.top"),sQuery(id+"F18.wireOp",EDGE,"E24.right"),sQuery(id+"F20.wireOp",EDGE,"E26.top"),sQuery(id+"F20.wireOp",EDGE,"E26.left")])]});
            var Q35;
            Q35=makeQuery(id+"FFzUMfXQeQxxDpQ_17.opExtrude","SWEPT_EDGE",EDGE,{"disambiguationData":[OSD([sQuery(id+"F12.wireOp",EDGE,"E21.bottom"),sQuery(id+"F12.wireOp",EDGE,"E21.right"),sQuery(id+"F18.wireOp",EDGE,"E24.bottom"),sQuery(id+"F18.wireOp",EDGE,"E24.right"),sQuery(id+"F20.wireOp",EDGE,"E26.bottom"),sQuery(id+"F20.wireOp",EDGE,"E26.right")])]});
            var Q36;
            Q36=makeQuery(id+"F19.opExtrude","SWEPT_EDGE",EDGE,{"disambiguationData":[OSD([sQuery(id+"F12.wireOp",EDGE,"E21.bottom"),sQuery(id+"F12.wireOp",EDGE,"E21.right"),sQuery(id+"F18.wireOp",EDGE,"E24.bottom"),sQuery(id+"F18.wireOp",EDGE,"E24.left")])]});
            var Q37;
            Q37=makeQuery(id+"F19.opExtrude","SWEPT_EDGE",EDGE,{"disambiguationData":[OSD([sQuery(id+"F0.wireOp",EDGE,"E12.MirrorCS"),sQuery(id+"F0.wireOp",EDGE,"E13.MirrorCS"),sQuery(id+"F12.wireOp",EDGE,"E21.top"),sQuery(id+"F12.wireOp",EDGE,"E21.right"),sQuery(id+"F18.wireOp",EDGE,"E24.top"),sQuery(id+"F18.wireOp",EDGE,"E24.left")])]});
            var Q38;
            Q38=makeQuery(id+"F15.opExtrude","SWEPT_EDGE",EDGE,{"disambiguationData":[OSD([sQuery(id+"F14.wireOp",EDGE,"E22.bottom"),sQuery(id+"F14.wireOp",EDGE,"E22.right")])]});
            var Q39;
            Q39=makeQuery(id+"F15.opExtrude","SWEPT_EDGE",EDGE,{"disambiguationData":[OSD([sQuery(id+"F14.wireOp",EDGE,"E22.bottom"),sQuery(id+"F14.wireOp",EDGE,"E22.left")])]});
            var Q40;
            Q40=makeQuery(id+"F15.opExtrude","SWEPT_EDGE",EDGE,{"disambiguationData":[OSD([sQuery(id+"F0.wireOp",EDGE,"E9.MirrorCS"),sQuery(id+"F0.wireOp",EDGE,"E10.MirrorCS"),sQuery(id+"F14.wireOp",EDGE,"E22.top"),sQuery(id+"F14.wireOp",EDGE,"E22.left")])]});
            var Q41;
            Q41=makeQuery(id+"F1.opExtrude","SWEPT_EDGE",EDGE,{"disambiguationData":[OSD([sQuery(id+"F0.wireOp",EDGE,"E9.MirrorCS"),sQuery(id+"F0.wireOp",EDGE,"E10.MirrorCS")])]});
            var Q42;
            Q42=makeQuery(id+"F1.opExtrude","SWEPT_EDGE",EDGE,{"disambiguationData":[OSD([sQuery(id+"F0.wireOp",EDGE,"E10.MirrorCS"),sQuery(id+"F0.wireOp",EDGE,"E11.MirrorCS")])]});
            var Q43;
            Q43=makeQuery(id+"F9.opExtrude","SWEPT_EDGE",EDGE,{"disambiguationData":[OSD([sQuery(id+"F0.wireOp",EDGE,"E9.MirrorCS"),sQuery(id+"F0.wireOp",EDGE,"E10.MirrorCS"),sQuery(id+"F8.wireOp",EDGE,"E19.bottom"),sQuery(id+"F8.wireOp",EDGE,"E19.right")])]});
            var Q44;
            Q44=makeQuery(id+"F1.opExtrude","SWEPT_EDGE",EDGE,{"disambiguationData":[OSD([sQuery(id+"F0.wireOp",EDGE,"E8.MirrorCS"),sQuery(id+"F0.wireOp",EDGE,"E9.MirrorCS")])]});
            var Q45;
            Q45=makeQuery(id+"F3.opExtrude","SWEPT_EDGE",EDGE,{"disambiguationData":[OSD([sQuery(id+"F0.wireOp",EDGE,"E13.MirrorCS"),sQuery(id+"F0.wireOp",EDGE,"E14.MirrorCS"),sQuery(id+"F2.wireOp",EDGE,"E16.bottom"),sQuery(id+"F2.wireOp",EDGE,"E16.right")])]});
            var Q46;
            Q46=makeQuery(id+"F3.opExtrude","SWEPT_EDGE",EDGE,{"disambiguationData":[OSD([sQuery(id+"F0.wireOp",EDGE,"E13.MirrorCS"),sQuery(id+"F0.wireOp",EDGE,"E14.MirrorCS"),sQuery(id+"F2.wireOp",EDGE,"E16.top"),sQuery(id+"F2.wireOp",EDGE,"E16.right")])]});
            var Q47;
            Q47=makeQuery(id+"FFzUMfXQeQxxDpQ_17.opExtrude","SWEPT_EDGE",EDGE,{"disambiguationData":[OSD([sQuery(id+"F12.wireOp",EDGE,"E21.bottom"),sQuery(id+"F12.wireOp",EDGE,"E21.right"),sQuery(id+"F18.wireOp",EDGE,"E24.bottom"),sQuery(id+"F18.wireOp",EDGE,"E24.right"),sQuery(id+"F20.wireOp",EDGE,"E27.bottom"),sQuery(id+"F20.wireOp",EDGE,"E27.right")])]});
            var Q48;
            Q48=makeQuery(id+"FFzUMfXQeQxxDpQ_17.opExtrude","SWEPT_EDGE",EDGE,{"disambiguationData":[OSD([sQuery(id+"F12.wireOp",EDGE,"E21.bottom"),sQuery(id+"F12.wireOp",EDGE,"E21.right"),sQuery(id+"F18.wireOp",EDGE,"E24.bottom"),sQuery(id+"F18.wireOp",EDGE,"E24.right"),sQuery(id+"F20.wireOp",EDGE,"E27.bottom"),sQuery(id+"F20.wireOp",EDGE,"E27.left")])]});
            var Q49;
            Q49=makeQuery(id+"FFzUMfXQeQxxDpQ_17.opExtrude","SWEPT_EDGE",EDGE,{"disambiguationData":[OSD([sQuery(id+"F0.wireOp",EDGE,"E12.MirrorCS"),sQuery(id+"F0.wireOp",EDGE,"E13.MirrorCS"),sQuery(id+"F12.wireOp",EDGE,"E21.top"),sQuery(id+"F12.wireOp",EDGE,"E21.right"),sQuery(id+"F18.wireOp",EDGE,"E24.top"),sQuery(id+"F18.wireOp",EDGE,"E24.right"),sQuery(id+"F20.wireOp",EDGE,"E27.top"),sQuery(id+"F20.wireOp",EDGE,"E27.right")])]});
            var Q50;
            Q50=makeQuery(id+"F19.opExtrude","SWEPT_EDGE",EDGE,{"disambiguationData":[OSD([sQuery(id+"F0.wireOp",EDGE,"E12.MirrorCS"),sQuery(id+"F0.wireOp",EDGE,"E13.MirrorCS"),sQuery(id+"F12.wireOp",EDGE,"E21.top"),sQuery(id+"F12.wireOp",EDGE,"E21.right"),sQuery(id+"F18.wireOp",EDGE,"E25.top"),sQuery(id+"F18.wireOp",EDGE,"E25.left")])]});
            var Q51;
            Q51=makeQuery(id+"F25.opExtrude","SWEPT_EDGE",EDGE,{"disambiguationData":[OSD([sQuery(id+"F24.wireOp",EDGE,"E32.bottom"),sQuery(id+"F24.wireOp",EDGE,"E32.right")])]});
            var Q52;
            Q52=makeQuery(id+"F25.opExtrude","SWEPT_EDGE",EDGE,{"disambiguationData":[OSD([sQuery(id+"F12.wireOp",EDGE,"E21.bottom"),sQuery(id+"F12.wireOp",EDGE,"E21.right"),sQuery(id+"F18.wireOp",EDGE,"E24.bottom"),sQuery(id+"F18.wireOp",EDGE,"E24.left"),sQuery(id+"F21.wireOp",EDGE,"E29.bottom"),sQuery(id+"F21.wireOp",EDGE,"E29.right"),sQuery(id+"F24.wireOp",EDGE,"E32.top"),sQuery(id+"F24.wireOp",EDGE,"E32.right")])]});
            var Q53;
            Q53=makeQuery(id+"F25.opExtrude","SWEPT_EDGE",EDGE,{"disambiguationData":[OSD([sQuery(id+"F24.wireOp",EDGE,"E32.bottom"),sQuery(id+"F24.wireOp",EDGE,"E32.left")])]});
            var Q54;
            Q54=makeQuery(id+"F23.opExtrude","SWEPT_EDGE",EDGE,{"disambiguationData":[OSD([sQuery(id+"F12.wireOp",EDGE,"E21.bottom"),sQuery(id+"F12.wireOp",EDGE,"E21.right"),sQuery(id+"F18.wireOp",EDGE,"E24.bottom"),sQuery(id+"F18.wireOp",EDGE,"E24.left"),sQuery(id+"F21.wireOp",EDGE,"E29.bottom"),sQuery(id+"F21.wireOp",EDGE,"E29.right")])]});
            var Q55;
            Q55=makeQuery(id+"F23.opExtrude","SWEPT_EDGE",EDGE,{"disambiguationData":[OSD([sQuery(id+"F12.wireOp",EDGE,"E21.bottom"),sQuery(id+"F12.wireOp",EDGE,"E21.right"),sQuery(id+"F18.wireOp",EDGE,"E24.bottom"),sQuery(id+"F18.wireOp",EDGE,"E24.left"),sQuery(id+"F21.wireOp",EDGE,"E29.top"),sQuery(id+"F21.wireOp",EDGE,"E29.right")])]});
            var Q56;
            Q56=makeQuery(id+"F23.opExtrude","SWEPT_EDGE",EDGE,{"disambiguationData":[OSD([sQuery(id+"F12.wireOp",EDGE,"E21.bottom"),sQuery(id+"F12.wireOp",EDGE,"E21.right"),sQuery(id+"F18.wireOp",EDGE,"E24.bottom"),sQuery(id+"F18.wireOp",EDGE,"E24.left"),sQuery(id+"F21.wireOp",EDGE,"E28.bottom"),sQuery(id+"F21.wireOp",EDGE,"E28.right")])]});
            var Q57;
            Q57=makeQuery(id+"F23.opExtrude","SWEPT_EDGE",EDGE,{"disambiguationData":[OSD([sQuery(id+"F12.wireOp",EDGE,"E21.bottom"),sQuery(id+"F12.wireOp",EDGE,"E21.right"),sQuery(id+"F18.wireOp",EDGE,"E24.bottom"),sQuery(id+"F18.wireOp",EDGE,"E24.left"),sQuery(id+"F21.wireOp",EDGE,"E28.top"),sQuery(id+"F21.wireOp",EDGE,"E28.right")])]});
            var Q58;
            Q58=makeQuery(id+"F23.opExtrude","SWEPT_EDGE",EDGE,{"disambiguationData":[OSD([sQuery(id+"F12.wireOp",EDGE,"E21.bottom"),sQuery(id+"F12.wireOp",EDGE,"E21.right"),sQuery(id+"F18.wireOp",EDGE,"E24.bottom"),sQuery(id+"F18.wireOp",EDGE,"E24.right"),sQuery(id+"F21.wireOp",EDGE,"E28.bottom"),sQuery(id+"F21.wireOp",EDGE,"E28.left")])]});
            var Q59;
            Q59=makeQuery(id+"F23.opExtrude","SWEPT_EDGE",EDGE,{"disambiguationData":[OSD([sQuery(id+"F12.wireOp",EDGE,"E21.bottom"),sQuery(id+"F12.wireOp",EDGE,"E21.right"),sQuery(id+"F18.wireOp",EDGE,"E24.bottom"),sQuery(id+"F18.wireOp",EDGE,"E24.right"),sQuery(id+"F21.wireOp",EDGE,"E29.bottom"),sQuery(id+"F21.wireOp",EDGE,"E29.left")])]});
            var Q60;
            Q60=makeQuery(id+"F23.opExtrude","SWEPT_EDGE",EDGE,{"disambiguationData":[OSD([sQuery(id+"F12.wireOp",EDGE,"E21.bottom"),sQuery(id+"F12.wireOp",EDGE,"E21.right"),sQuery(id+"F18.wireOp",EDGE,"E24.bottom"),sQuery(id+"F18.wireOp",EDGE,"E24.right"),sQuery(id+"F21.wireOp",EDGE,"E29.top"),sQuery(id+"F21.wireOp",EDGE,"E29.left")])]});
            var Q61;
            Q61=makeQuery(id+"F25.opExtrude","SWEPT_EDGE",EDGE,{"disambiguationData":[OSD([sQuery(id+"F12.wireOp",EDGE,"E21.bottom"),sQuery(id+"F12.wireOp",EDGE,"E21.right"),sQuery(id+"F18.wireOp",EDGE,"E24.bottom"),sQuery(id+"F18.wireOp",EDGE,"E24.right"),sQuery(id+"F21.wireOp",EDGE,"E29.bottom"),sQuery(id+"F21.wireOp",EDGE,"E29.left"),sQuery(id+"F24.wireOp",EDGE,"E32.top"),sQuery(id+"F24.wireOp",EDGE,"E32.left")])]});
            var Q62;
            Q62=makeQuery(id+"F23.opExtrude","SWEPT_EDGE",EDGE,{"disambiguationData":[OSD([sQuery(id+"F12.wireOp",EDGE,"E21.bottom"),sQuery(id+"F12.wireOp",EDGE,"E21.right"),sQuery(id+"F18.wireOp",EDGE,"E24.bottom"),sQuery(id+"F18.wireOp",EDGE,"E24.right"),sQuery(id+"F21.wireOp",EDGE,"E28.top"),sQuery(id+"F21.wireOp",EDGE,"E28.left")])]});
            var Q63;
            Q63=makeQuery(id+"F23.opExtrude","SWEPT_EDGE",EDGE,{"disambiguationData":[OSD([sQuery(id+"F12.wireOp",EDGE,"E21.bottom"),sQuery(id+"F12.wireOp",EDGE,"E21.right"),sQuery(id+"F18.wireOp",EDGE,"E25.bottom"),sQuery(id+"F18.wireOp",EDGE,"E25.right"),sQuery(id+"F22.wireOp",EDGE,"E31.bottom"),sQuery(id+"F22.wireOp",EDGE,"E31.right")])]});
            var Q64;
            Q64=makeQuery(id+"F23.opExtrude","SWEPT_EDGE",EDGE,{"disambiguationData":[OSD([sQuery(id+"F12.wireOp",EDGE,"E21.bottom"),sQuery(id+"F12.wireOp",EDGE,"E21.right"),sQuery(id+"F18.wireOp",EDGE,"E25.bottom"),sQuery(id+"F18.wireOp",EDGE,"E25.right"),sQuery(id+"F22.wireOp",EDGE,"E31.top"),sQuery(id+"F22.wireOp",EDGE,"E31.right")])]});
            var Q65;
            Q65=makeQuery(id+"F23.opExtrude","SWEPT_EDGE",EDGE,{"disambiguationData":[OSD([sQuery(id+"F12.wireOp",EDGE,"E21.bottom"),sQuery(id+"F12.wireOp",EDGE,"E21.right"),sQuery(id+"F18.wireOp",EDGE,"E25.bottom"),sQuery(id+"F18.wireOp",EDGE,"E25.left"),sQuery(id+"F22.wireOp",EDGE,"E31.bottom"),sQuery(id+"F22.wireOp",EDGE,"E31.left")])]});
            var Q66;
            Q66=makeQuery(id+"F23.opExtrude","SWEPT_EDGE",EDGE,{"disambiguationData":[OSD([sQuery(id+"F12.wireOp",EDGE,"E21.bottom"),sQuery(id+"F12.wireOp",EDGE,"E21.right"),sQuery(id+"F18.wireOp",EDGE,"E25.bottom"),sQuery(id+"F18.wireOp",EDGE,"E25.left"),sQuery(id+"F22.wireOp",EDGE,"E31.top"),sQuery(id+"F22.wireOp",EDGE,"E31.left")])]});
            var Q67;
            Q67=makeQuery(id+"F27.opExtrude","SWEPT_EDGE",EDGE,{"disambiguationData":[OSD([sQuery(id+"F12.wireOp",EDGE,"E21.bottom"),sQuery(id+"F12.wireOp",EDGE,"E21.right"),sQuery(id+"F18.wireOp",EDGE,"E25.bottom"),sQuery(id+"F18.wireOp",EDGE,"E25.left"),sQuery(id+"F22.wireOp",EDGE,"E30.bottom"),sQuery(id+"F22.wireOp",EDGE,"E30.left"),sQuery(id+"F26.wireOp",EDGE,"E33.top"),sQuery(id+"F26.wireOp",EDGE,"E33.right")])]});
            var Q68;
            Q68=makeQuery(id+"F23.opExtrude","SWEPT_EDGE",EDGE,{"disambiguationData":[OSD([sQuery(id+"F12.wireOp",EDGE,"E21.bottom"),sQuery(id+"F12.wireOp",EDGE,"E21.right"),sQuery(id+"F18.wireOp",EDGE,"E25.bottom"),sQuery(id+"F18.wireOp",EDGE,"E25.left"),sQuery(id+"F22.wireOp",EDGE,"E30.bottom"),sQuery(id+"F22.wireOp",EDGE,"E30.left")])]});
            var Q69;
            Q69=makeQuery(id+"F23.opExtrude","SWEPT_EDGE",EDGE,{"disambiguationData":[OSD([sQuery(id+"F12.wireOp",EDGE,"E21.bottom"),sQuery(id+"F12.wireOp",EDGE,"E21.right"),sQuery(id+"F18.wireOp",EDGE,"E25.bottom"),sQuery(id+"F18.wireOp",EDGE,"E25.left"),sQuery(id+"F22.wireOp",EDGE,"E30.top"),sQuery(id+"F22.wireOp",EDGE,"E30.left")])]});
            fillet(context, id + "F45", {"entities" : qUnion([Q0, Q1, Q2, Q3, Q4, Q5, Q6, Q7, Q8, Q9, Q10, Q11, Q12, Q13, Q14, Q15, Q16, Q17, Q18, Q19, Q20, Q21, Q22, Q23, Q24, Q25, Q26, Q27, Q28, Q29, Q30, Q31, Q32, Q33, Q34, Q35, Q36, Q37, Q38, Q39, Q40, Q41, Q42, Q43, Q44, Q45, Q46, Q47, Q48, Q49, Q50, Q51, Q52, Q53, Q54, Q55, Q56, Q57, Q58, Q59, Q60, Q61, Q62, Q63, Q64, Q65, Q66, Q67, Q68, Q69]), "radius" : 2 * mm, "tangentPropagation" : true, "allowEdgeOverflow" : false});
        }
        {
            var Q0;
            Q0=makeQuery(id+"F11.opExtrude","SWEPT_EDGE",EDGE,{"disambiguationData":[OSD([sQuery(id+"F0.wireOp",EDGE,"E4.MirrorCS"),sQuery(id+"F0.wireOp",EDGE,"E5.MirrorCS"),sQuery(id+"F10.wireOp",EDGE,"E20.top"),sQuery(id+"F10.wireOp",EDGE,"E20.right")])]});
            var Q1;
            Q1=makeQuery(id+"F17.opExtrude","SWEPT_EDGE",EDGE,{"disambiguationData":[OSD([sQuery(id+"F0.wireOp",EDGE,"E1.top"),sQuery(id+"F0.wireOp",EDGE,"E1.left"),sQuery(id+"F16.wireOp",EDGE,"E23.top"),sQuery(id+"F16.wireOp",EDGE,"E23.right")])]});
            var Q2;
            Q2=makeQuery(id+"F15.opExtrude","SWEPT_EDGE",EDGE,{"disambiguationData":[OSD([sQuery(id+"F0.wireOp",EDGE,"E10.MirrorCS"),sQuery(id+"F0.wireOp",EDGE,"E11.MirrorCS"),sQuery(id+"F14.wireOp",EDGE,"E22.top"),sQuery(id+"F14.wireOp",EDGE,"E22.right")])]});
            fillet(context, id + "F46", {"entities" : qUnion([Q0, Q1, Q2]), "radius" : 2 * mm, "tangentPropagation" : true, "allowEdgeOverflow" : false});
        }
        {
            var Q0;
            Q0=makeQuery(id+"F19.opExtrude","SWEPT_FACE",FACE,{"disambiguationData":[OSD([sQuery(id+"F18.wireOp",EDGE,"E24.left")])]});
            var sketch = newSketch(context, id + "F47", { "sketchPlane" : qUnion([Q0])});
            skLineSegment(sketch, "E37.bottom", {"start": v(-55, 900) * mm, "end": v(-85, 900) * mm});
            skLineSegment(sketch, "E37.top", {"start": v(-55, 870) * mm, "end": v(-85, 870) * mm});
            skLineSegment(sketch, "E37.left", {"start": v(-55, 900) * mm, "end": v(-55, 870) * mm});
            skLineSegment(sketch, "E37.right", {"start": v(-85, 900) * mm, "end": v(-85, 870) * mm});
            skPoint(sketch, "E37.middle", {"position": v(-70, 885) * mm});
            skPoint(sketch, "E38.middle", {"position": v(210, 885) * mm});
            skLineSegment(sketch, "E39.bottom", {"start": v(225, 900) * mm, "end": v(195, 900) * mm});
            skLineSegment(sketch, "E39.top", {"start": v(225, 870) * mm, "end": v(195, 870) * mm});
            skLineSegment(sketch, "E39.left", {"start": v(225, 900) * mm, "end": v(225, 870) * mm});
            skLineSegment(sketch, "E39.right", {"start": v(195, 900) * mm, "end": v(195, 870) * mm});
            skSolve(sketch);
        }
        {
            var Q0;
            Q0=sQuery(id+"F47.wireOp",EDGE,"E37.bottom");
            var Q1;
            Q1=sQuery(id+"F47.wireOp",EDGE,"E37.right");
            var Q2;
            Q2=sQuery(id+"F47.wireOp",EDGE,"E37.top");
            var Q3;
            Q3=sQuery(id+"F47.wireOp",EDGE,"E37.left");
            extrude(context, id + "F48", {"bodyType" : ToolBodyType.SURFACE, "surfaceEntities" : qUnion([Q0, Q1, Q2, Q3]), "depth" : 115 * mm, "offsetDistance" : 25 * mm});
        }
        {
            var Q0;
            Q0=makeQuery(id+"F48.opExtrude","SWEPT_EDGE",EDGE,{"disambiguationData":[OSD([sQuery(id+"F47.wireOp",VERTEX,"E37.right.start")])]});
            var Q1;
            Q1=makeQuery(id+"F48.opExtrude","SWEPT_EDGE",EDGE,{"disambiguationData":[OSD([sQuery(id+"F47.wireOp",VERTEX,"E37.left.start")])]});
            var Q2;
            Q2=makeQuery(id+"F48.opExtrude","SWEPT_EDGE",EDGE,{"disambiguationData":[OSD([sQuery(id+"F47.wireOp",VERTEX,"E37.left.end")])]});
            var Q3;
            Q3=makeQuery(id+"FLmcnG1oEssqkVO_29.opExtrude","SWEPT_EDGE",EDGE,{"disambiguationData":[OSD([sQuery(id+"F47.wireOp",VERTEX,"E38.left.start")])]});
            var Q4;
            Q4=makeQuery(id+"F48.opExtrude","SWEPT_EDGE",EDGE,{"disambiguationData":[OSD([sQuery(id+"F47.wireOp",VERTEX,"E37.top.end")])]});
            var Q5;
            Q5=makeQuery(id+"FLmcnG1oEssqkVO_29.opExtrude","SWEPT_EDGE",EDGE,{"disambiguationData":[OSD([sQuery(id+"F47.wireOp",VERTEX,"E38.top.start")])]});
            var Q6;
            Q6=makeQuery(id+"FLmcnG1oEssqkVO_29.opExtrude","SWEPT_EDGE",EDGE,{"disambiguationData":[OSD([sQuery(id+"F47.wireOp",VERTEX,"E38.top.end")])]});
            var Q7;
            Q7=makeQuery(id+"FLmcnG1oEssqkVO_29.opExtrude","SWEPT_EDGE",EDGE,{"disambiguationData":[OSD([sQuery(id+"F47.wireOp",VERTEX,"E38.bottom.end")])]});
            fillet(context, id + "F49", {"entities" : qUnion([Q0, Q1, Q2, Q3, Q4, Q5, Q6, Q7]), "radius" : 2 * mm, "tangentPropagation" : true, "allowEdgeOverflow" : false});
        }
        {
            var Q0;
            Q0=makeQuery(id+"F33.opExtrude","CAP_FACE",FACE,{"disambiguationData":[OSD([sQuery(id+"F32.wireOp",EDGE,"E34.bottom"),sQuery(id+"F32.wireOp",EDGE,"E34.top"),sQuery(id+"F32.wireOp",EDGE,"E34.left"),sQuery(id+"F32.wireOp",EDGE,"E34.right")])],"isStart":true});
            var sketch = newSketch(context, id + "F50", { "sketchPlane" : qUnion([Q0])});
            skLineSegment(sketch, "E40", {"start": v(-70, 1115.4) * mm, "end": v(-70, 902.67) * mm, "construction": true});
            skLineSegment(sketch, "E41", {"start": v(-195, 1005.4) * mm, "end": v(46.57, 1005.4) * mm, "construction": true});
            skPoint(sketch, "E42", {"position": v(-70, 1005.4) * mm});
            skCircle(sketch, "E43", {"center": v(-70, 1005.4) * mm, "radius": 85 * mm, "construction": true});
            skLineSegment(sketch, "E44", {"start": v(-70, 1005.4) * mm, "end": v(-102.53, 1083.93) * mm, "construction": true});
            skLineSegment(sketch, "E45", {"start": v(-70, 1005.4) * mm, "end": v(-37.47, 1083.93) * mm, "construction": true});
            skLineSegment(sketch, "E46", {"start": v(-70, 1005.4) * mm, "end": v(-102.53, 926.87) * mm, "construction": true});
            skLineSegment(sketch, "E47", {"start": v(-70, 1005.4) * mm, "end": v(8.53, 972.88) * mm, "construction": true});
            skLineSegment(sketch, "E48", {"start": v(-70, 1005.4) * mm, "end": v(-148.53, 1037.93) * mm, "construction": true});
            skCircle(sketch, "E49", {"center": v(-37.47, 1083.93) * mm, "radius": 11 * mm, "construction": true});
            skCircle(sketch, "E50", {"center": v(-148.53, 1037.93) * mm, "radius": 11 * mm, "construction": true});
            skCircle(sketch, "E51", {"center": v(8.53, 972.88) * mm, "radius": 11 * mm, "construction": true});
            skCircle(sketch, "E52", {"center": v(-102.53, 926.87) * mm, "radius": 11 * mm, "construction": true});
            skSolve(sketch);
        }
        {
            var Q0;
            Q0 = qSketchRegion(id + "F47", true);
            extrude(context, id + "F51", {"entities" : qUnion([Q0]), "endBound" : BoundingType.UP_TO_NEXT, "depth" : 25 * mm, "offsetDistance" : 25 * mm});
        }
        {
            var Q0;
            Q0=makeQuery(id+"F51.opExtrude","SWEPT_EDGE",EDGE,{"disambiguationData":[OSD([sQuery(id+"F47.wireOp",EDGE,"E39.bottom"),sQuery(id+"F47.wireOp",EDGE,"E39.left")])]});
            var Q1;
            Q1=makeQuery(id+"F51.opExtrude","SWEPT_EDGE",EDGE,{"disambiguationData":[OSD([sQuery(id+"F47.wireOp",EDGE,"E39.bottom"),sQuery(id+"F47.wireOp",EDGE,"E39.right")])]});
            var Q2;
            Q2=makeQuery(id+"F51.opExtrude","SWEPT_EDGE",EDGE,{"disambiguationData":[OSD([sQuery(id+"F47.wireOp",EDGE,"E39.top"),sQuery(id+"F47.wireOp",EDGE,"E39.left")])]});
            var Q3;
            Q3=makeQuery(id+"F51.opExtrude","SWEPT_EDGE",EDGE,{"disambiguationData":[OSD([sQuery(id+"F47.wireOp",EDGE,"E39.top"),sQuery(id+"F47.wireOp",EDGE,"E39.right")])]});
            fillet(context, id + "F52", {"entities" : qUnion([Q0, Q1, Q2, Q3]), "radius" : 2 * mm, "tangentPropagation" : true, "allowEdgeOverflow" : false});
        }
        {
            var Q0;
            Q0=makeQuery(id+"F19.opExtrude","SWEPT_FACE",FACE,{"disambiguationData":[OSD([sQuery(id+"F18.wireOp",EDGE,"E25.right")])]});
            var sketch = newSketch(context, id + "F53", { "sketchPlane" : qUnion([Q0])});
            skLineSegment(sketch, "E53.bottom", {"start": v(85, 900) * mm, "end": v(55, 900) * mm});
            skLineSegment(sketch, "E53.top", {"start": v(85, 870) * mm, "end": v(55, 870) * mm});
            skLineSegment(sketch, "E53.left", {"start": v(85, 900) * mm, "end": v(85, 870) * mm});
            skLineSegment(sketch, "E53.right", {"start": v(55, 900) * mm, "end": v(55, 870) * mm});
            skPoint(sketch, "E53.middle", {"position": v(70, 885) * mm});
            skLineSegment(sketch, "E54.bottom", {"start": v(-195, 900) * mm, "end": v(-225, 900) * mm});
            skLineSegment(sketch, "E54.top", {"start": v(-195, 870) * mm, "end": v(-225, 870) * mm});
            skLineSegment(sketch, "E54.left", {"start": v(-195, 900) * mm, "end": v(-195, 870) * mm});
            skLineSegment(sketch, "E54.right", {"start": v(-225, 900) * mm, "end": v(-225, 870) * mm});
            skPoint(sketch, "E54.middle", {"position": v(-210, 885) * mm});
            skSolve(sketch);
        }
        {
            var Q0;
            Q0 = qSketchRegion(id + "F53", true);
            extrude(context, id + "F54", {"entities" : qUnion([Q0]), "endBound" : BoundingType.UP_TO_NEXT, "depth" : 25 * mm, "offsetDistance" : 25 * mm});
        }
        {
            var Q0;
            Q0=makeQuery(id+"F54.opExtrude","SWEPT_EDGE",EDGE,{"disambiguationData":[OSD([sQuery(id+"F53.wireOp",EDGE,"E54.bottom"),sQuery(id+"F53.wireOp",EDGE,"E54.left")])]});
            var Q1;
            Q1=makeQuery(id+"F54.opExtrude","SWEPT_EDGE",EDGE,{"disambiguationData":[OSD([sQuery(id+"F53.wireOp",EDGE,"E54.bottom"),sQuery(id+"F53.wireOp",EDGE,"E54.right")])]});
            var Q2;
            Q2=makeQuery(id+"F54.opExtrude","SWEPT_EDGE",EDGE,{"disambiguationData":[OSD([sQuery(id+"F53.wireOp",EDGE,"E54.top"),sQuery(id+"F53.wireOp",EDGE,"E54.right")])]});
            var Q3;
            Q3=makeQuery(id+"F54.opExtrude","SWEPT_EDGE",EDGE,{"disambiguationData":[OSD([sQuery(id+"F53.wireOp",EDGE,"E54.top"),sQuery(id+"F53.wireOp",EDGE,"E54.left")])]});
            var Q4;
            Q4=makeQuery(id+"F54.opExtrude","SWEPT_EDGE",EDGE,{"disambiguationData":[OSD([sQuery(id+"F53.wireOp",EDGE,"E53.top"),sQuery(id+"F53.wireOp",EDGE,"E53.right")])]});
            var Q5;
            Q5=makeQuery(id+"F54.opExtrude","SWEPT_EDGE",EDGE,{"disambiguationData":[OSD([sQuery(id+"F53.wireOp",EDGE,"E53.top"),sQuery(id+"F53.wireOp",EDGE,"E53.left")])]});
            var Q6;
            Q6=makeQuery(id+"F54.opExtrude","SWEPT_EDGE",EDGE,{"disambiguationData":[OSD([sQuery(id+"F53.wireOp",EDGE,"E53.bottom"),sQuery(id+"F53.wireOp",EDGE,"E53.left")])]});
            var Q7;
            Q7=makeQuery(id+"F54.opExtrude","SWEPT_EDGE",EDGE,{"disambiguationData":[OSD([sQuery(id+"F53.wireOp",EDGE,"E53.bottom"),sQuery(id+"F53.wireOp",EDGE,"E53.right")])]});
            fillet(context, id + "F55", {"entities" : qUnion([Q0, Q1, Q2, Q3, Q4, Q5, Q6, Q7]), "radius" : 2 * mm, "tangentPropagation" : true, "allowEdgeOverflow" : false});
        }
        {
            var Q0;
            Q0=sQuery(id+"F50.wireOp",VERTEX,"E45.end");
            var Q1;
            Q1=sQuery(id+"F50.wireOp",VERTEX,"E47.end");
            var Q2;
            Q2=sQuery(id+"F50.wireOp",VERTEX,"E46.end");
            var Q3;
            Q3=sQuery(id+"F50.wireOp",VERTEX,"E48.end");
            var Q4;
            Q4=makeQuery(id+"F40.opExtrude","SWEPT_BODY",BODY,{"disambiguationData":[OSD([sQuery(id+"F39.wireOp",EDGE,"E35.bottom"),sQuery(id+"F39.wireOp",EDGE,"E35.top"),sQuery(id+"F39.wireOp",EDGE,"E35.left"),sQuery(id+"F39.wireOp",EDGE,"E35.right")])]});
            var Q5;
            Q5=makeQuery(id+"F33.opExtrude","SWEPT_BODY",BODY,{"disambiguationData":[OSD([sQuery(id+"F32.wireOp",EDGE,"E34.bottom"),sQuery(id+"F32.wireOp",EDGE,"E34.top"),sQuery(id+"F32.wireOp",EDGE,"E34.left"),sQuery(id+"F32.wireOp",EDGE,"E34.right")])]});
            hole(context, id + "F56", {"style" : HoleStyle.SIMPLE, "endStyle" : HoleEndStyle.THROUGH, "holeDiameter" : 22 * mm, "majorDiameter" : 5 * mm, "isTappedThrough" : true, "tappedDepth" : 12 * mm, "tapClearance" : 3, "locations" : qUnion([Q0, Q1, Q2, Q3]), "scope" : qUnion([Q4, Q5])});
        }
    });
